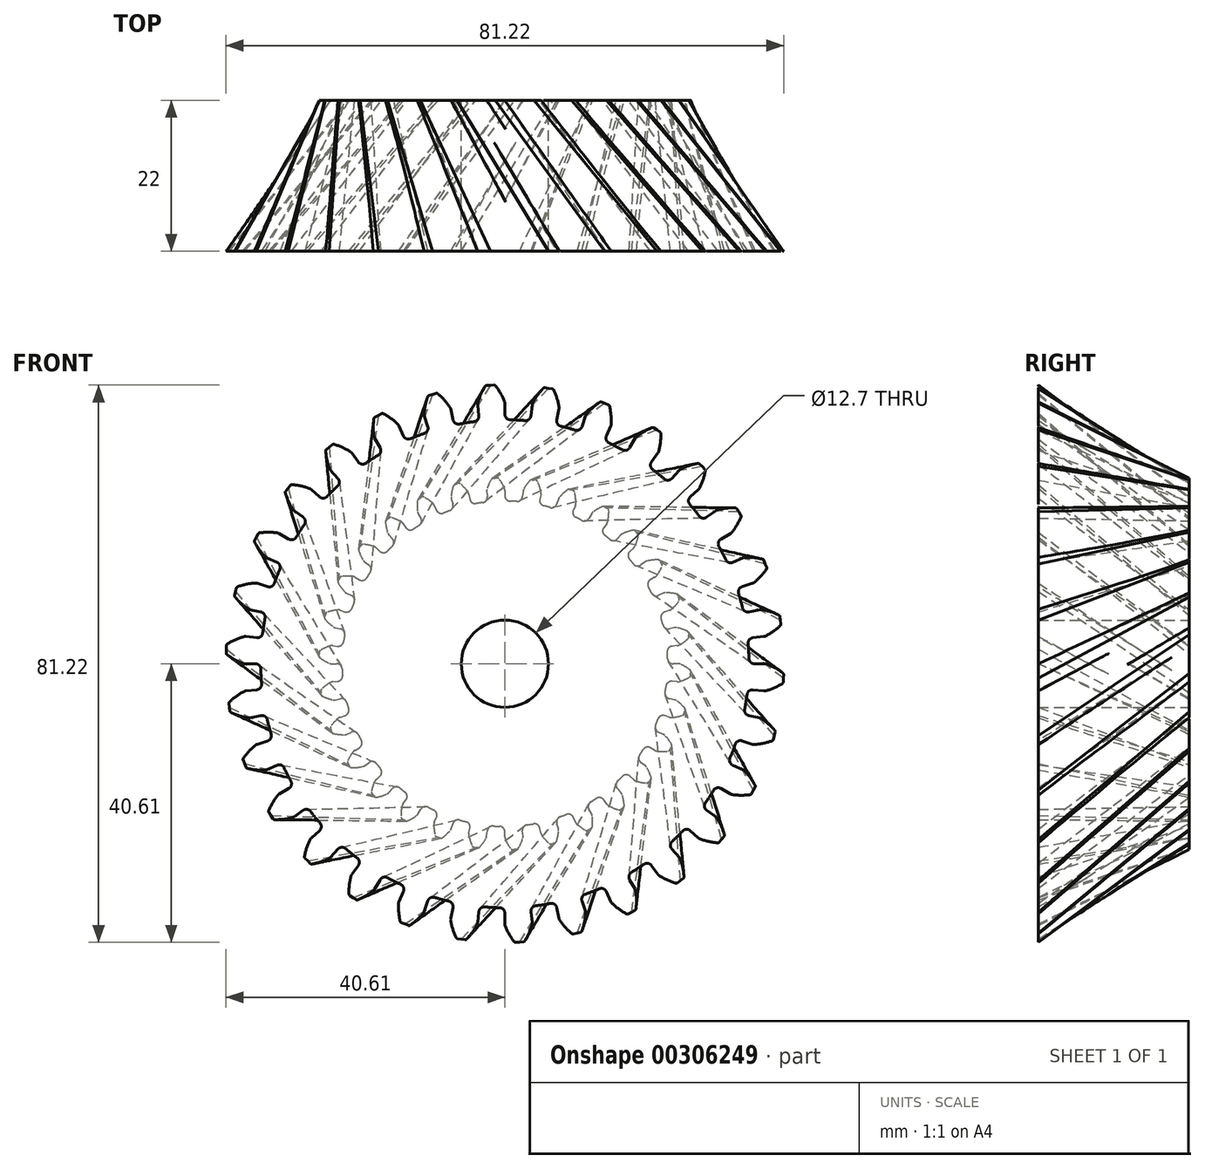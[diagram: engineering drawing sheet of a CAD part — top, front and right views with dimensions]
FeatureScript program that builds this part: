
annotation { "Feature Type Name" : "Feature", "Feature Type Description" : "" }
export const myFeature = defineFeature(function(context is Context, id is Id, definition is map)
    precondition{}
    {
        {
            var Q0;
            Q0=qCreatedBy(makeId("Front.planeOp"),FACE);
            var sketch = newSketch(context, id + "F0", { "sketchPlane" : qUnion([Q0])});
            skArc(sketch, "E0", {"start": v(-3.24, 23.49) * mm, "mid": v(-4.09, 23.36) * mm, "end": v(-4.93, 23.2) * mm});
            skArc(sketch, "E1.trimOffspring", {"start": v(-0.06, 25.55) * mm, "mid": v(-0.42, 26.29) * mm, "end": v(-0.88, 26.97) * mm});
            skLineSegment(sketch, "E2", {"start": v(-1.08, 27.07) * mm, "end": v(-1.42, 27.07) * mm});
            skLineSegment(sketch, "E3", {"start": v(0, 25.25) * mm, "end": v(0, 24.5) * mm});
            skLineSegment(sketch, "E4.MirrorCS", {"start": v(-1.76, 27.04) * mm, "end": v(-1.42, 27.07) * mm});
            skArc(sketch, "E5.MirrorCS", {"start": v(-2.61, 25.42) * mm, "mid": v(-2.33, 26.19) * mm, "end": v(-1.95, 26.92) * mm});
            skLineSegment(sketch, "E6.MirrorCS", {"start": v(-2.64, 25.1) * mm, "end": v(-2.56, 24.36) * mm});
            skArc(sketch, "E7.filletArc", {"start": v(-3.24, 23.49) * mm, "mid": v(-2.72, 23.79) * mm, "end": v(-2.56, 24.36) * mm});
            skPoint(sketch, "E8.visualSharp", {"position": v(0, 23.71) * mm});
            skPoint(sketch, "E9.visualSharp", {"position": v(-2.66, 25.26) * mm});
            skArc(sketch, "E9.filletArc", {"start": v(-2.65, 25.26) * mm, "mid": v(-2.65, 25.26) * mm, "end": v(-2.65, 25.26) * mm});
            skArc(sketch, "E10.filletArc", {"start": v(0, 24.5) * mm, "mid": v(0.22, 23.94) * mm, "end": v(0.77, 23.7) * mm});
            skArc(sketch, "E11.filletArc", {"start": v(-2.61, 25.42) * mm, "mid": v(-2.64, 25.26) * mm, "end": v(-2.64, 25.1) * mm});
            skPoint(sketch, "E12.visualSharp", {"position": v(0, 25.4) * mm});
            skArc(sketch, "E12.filletArc", {"start": v(0, 25.25) * mm, "mid": v(-0.02, 25.4) * mm, "end": v(-0.06, 25.55) * mm});
            skPoint(sketch, "E13.visualSharp", {"position": v(-1.88, 27.02) * mm});
            skArc(sketch, "E13.filletArc", {"start": v(-1.76, 27.04) * mm, "mid": v(-1.86, 27) * mm, "end": v(-1.95, 26.92) * mm});
            skPoint(sketch, "E14.visualSharp", {"position": v(-0.96, 27.07) * mm});
            skArc(sketch, "E14.filletArc", {"start": v(-0.88, 26.97) * mm, "mid": v(-0.97, 27.05) * mm, "end": v(-1.08, 27.07) * mm});
            skArc(sketch, "E15.1.0", {"start": v(-5.37, 24.98) * mm, "mid": v(-5.88, 25.63) * mm, "end": v(-6.47, 26.2) * mm});
            skPoint(sketch, "E15.1.1", {"position": v(-5.28, 24.84) * mm});
            skPoint(sketch, "E15.1.2", {"position": v(-7.85, 24.16) * mm});
            skLineSegment(sketch, "E15.1.3", {"start": v(-5.25, 24.7) * mm, "end": v(-5.1, 23.96) * mm});
            skArc(sketch, "E15.1.4", {"start": v(-7.84, 24.32) * mm, "mid": v(-7.72, 25.13) * mm, "end": v(-7.5, 25.92) * mm});
            skArc(sketch, "E15.1.5", {"start": v(-8.05, 22.3) * mm, "mid": v(-7.61, 22.7) * mm, "end": v(-7.57, 23.3) * mm});
            skPoint(sketch, "E15.1.6", {"position": v(-4.93, 23.2) * mm});
            skArc(sketch, "E15.1.7", {"start": v(-5.1, 23.96) * mm, "mid": v(-4.76, 23.46) * mm, "end": v(-4.18, 23.34) * mm});
            skPoint(sketch, "E15.1.8", {"position": v(-6.56, 26.28) * mm});
            skPoint(sketch, "E15.1.9", {"position": v(-7.46, 26.04) * mm});
            skLineSegment(sketch, "E15.1.10", {"start": v(-7.8, 24.01) * mm, "end": v(-7.57, 23.3) * mm});
            skArc(sketch, "E15.1.11", {"start": v(-5.25, 24.7) * mm, "mid": v(-5.3, 24.84) * mm, "end": v(-5.37, 24.98) * mm});
            skLineSegment(sketch, "E15.1.12", {"start": v(-7.34, 26.08) * mm, "end": v(-7.02, 26.19) * mm});
            skLineSegment(sketch, "E15.1.13", {"start": v(-6.69, 26.26) * mm, "end": v(-7.02, 26.19) * mm});
            skArc(sketch, "E15.1.14", {"start": v(-7.34, 26.08) * mm, "mid": v(-7.44, 26.02) * mm, "end": v(-7.5, 25.92) * mm});
            skArc(sketch, "E15.1.15", {"start": v(-6.47, 26.2) * mm, "mid": v(-6.57, 26.25) * mm, "end": v(-6.69, 26.26) * mm});
            skArc(sketch, "E15.1.16", {"start": v(-7.84, 24.32) * mm, "mid": v(-7.84, 24.16) * mm, "end": v(-7.8, 24.01) * mm});
            skArc(sketch, "E15.1.17", {"start": v(-7.85, 24.16) * mm, "mid": v(-7.85, 24.16) * mm, "end": v(-7.85, 24.15) * mm});
            skArc(sketch, "E15.1.18", {"start": v(-7.85, 24.16) * mm, "mid": v(-7.85, 24.16) * mm, "end": v(-7.85, 24.15) * mm});
            skArc(sketch, "E15.2.0", {"start": v(-10.45, 23.32) * mm, "mid": v(-11.08, 23.84) * mm, "end": v(-11.77, 24.28) * mm});
            skPoint(sketch, "E15.2.1", {"position": v(-10.33, 23.2) * mm});
            skPoint(sketch, "E15.2.2", {"position": v(-12.7, 22) * mm});
            skLineSegment(sketch, "E15.2.3", {"start": v(-10.27, 23.06) * mm, "end": v(-9.96, 22.37) * mm});
            skArc(sketch, "E15.2.4", {"start": v(-12.72, 22.16) * mm, "mid": v(-12.78, 22.98) * mm, "end": v(-12.73, 23.8) * mm});
            skArc(sketch, "E15.2.5", {"start": v(-12.51, 20.14) * mm, "mid": v(-12.16, 20.62) * mm, "end": v(-12.25, 21.21) * mm});
            skPoint(sketch, "E15.2.6", {"position": v(-9.64, 21.66) * mm});
            skArc(sketch, "E15.2.7", {"start": v(-9.96, 22.37) * mm, "mid": v(-9.53, 21.96) * mm, "end": v(-8.94, 21.96) * mm});
            skPoint(sketch, "E15.2.8", {"position": v(-11.88, 24.34) * mm});
            skPoint(sketch, "E15.2.9", {"position": v(-12.7, 23.92) * mm});
            skLineSegment(sketch, "E15.2.10", {"start": v(-12.62, 21.87) * mm, "end": v(-12.25, 21.21) * mm});
            skArc(sketch, "E15.2.11", {"start": v(-10.27, 23.06) * mm, "mid": v(-10.35, 23.2) * mm, "end": v(-10.45, 23.32) * mm});
            skLineSegment(sketch, "E15.2.12", {"start": v(-12.6, 23.99) * mm, "end": v(-12.3, 24.15) * mm});
            skLineSegment(sketch, "E15.2.13", {"start": v(-12, 24.3) * mm, "end": v(-12.3, 24.15) * mm});
            skArc(sketch, "E15.2.14", {"start": v(-12.6, 23.99) * mm, "mid": v(-12.68, 23.9) * mm, "end": v(-12.73, 23.8) * mm});
            skArc(sketch, "E15.2.15", {"start": v(-11.77, 24.28) * mm, "mid": v(-11.88, 24.31) * mm, "end": v(-12, 24.3) * mm});
            skArc(sketch, "E15.2.16", {"start": v(-12.72, 22.16) * mm, "mid": v(-12.69, 22) * mm, "end": v(-12.62, 21.87) * mm});
            skArc(sketch, "E15.2.17", {"start": v(-12.7, 22) * mm, "mid": v(-12.7, 22) * mm, "end": v(-12.7, 22) * mm});
            skArc(sketch, "E15.2.18", {"start": v(-12.7, 22) * mm, "mid": v(-12.7, 22) * mm, "end": v(-12.7, 22) * mm});
            skArc(sketch, "E16.1.3.0", {"start": v(-15.07, 20.64) * mm, "mid": v(-15.8, 21.02) * mm, "end": v(-16.56, 21.3) * mm});
            skPoint(sketch, "E16.4.3.0", {"position": v(-14.93, 20.55) * mm});
            skPoint(sketch, "E16.5.3.0", {"position": v(-17, 18.88) * mm});
            skLineSegment(sketch, "E16.6.3.0", {"start": v(-14.84, 20.43) * mm, "end": v(-14.4, 19.81) * mm});
            skArc(sketch, "E16.9.3.0", {"start": v(-17.05, 19.03) * mm, "mid": v(-17.28, 19.82) * mm, "end": v(-17.4, 20.63) * mm});
            skArc(sketch, "E16.13.3.0", {"start": v(-16.43, 17.1) * mm, "mid": v(-16.18, 17.64) * mm, "end": v(-16.39, 18.2) * mm});
            skPoint(sketch, "E16.17.3.0", {"position": v(-13.94, 19.18) * mm});
            skArc(sketch, "E16.18.3.0", {"start": v(-14.4, 19.81) * mm, "mid": v(-13.9, 19.5) * mm, "end": v(-13.3, 19.62) * mm});
            skPoint(sketch, "E16.22.3.0", {"position": v(-16.69, 21.34) * mm});
            skPoint(sketch, "E16.23.3.0", {"position": v(-17.4, 20.76) * mm});
            skLineSegment(sketch, "E16.24.3.0", {"start": v(-16.9, 18.76) * mm, "end": v(-16.39, 18.2) * mm});
            skArc(sketch, "E16.27.3.0", {"start": v(-14.84, 20.43) * mm, "mid": v(-14.94, 20.54) * mm, "end": v(-15.07, 20.64) * mm});
            skLineSegment(sketch, "E16.31.3.0", {"start": v(-17.31, 20.84) * mm, "end": v(-17.06, 21.07) * mm});
            skLineSegment(sketch, "E16.34.3.0", {"start": v(-16.79, 21.27) * mm, "end": v(-17.06, 21.07) * mm});
            skArc(sketch, "E16.37.3.0", {"start": v(-17.31, 20.84) * mm, "mid": v(-17.38, 20.75) * mm, "end": v(-17.4, 20.63) * mm});
            skArc(sketch, "E16.41.3.0", {"start": v(-16.56, 21.3) * mm, "mid": v(-16.68, 21.31) * mm, "end": v(-16.79, 21.27) * mm});
            skArc(sketch, "E16.45.3.0", {"start": v(-17.05, 19.03) * mm, "mid": v(-16.99, 18.89) * mm, "end": v(-16.9, 18.76) * mm});
            skArc(sketch, "E16.49.3.0", {"start": v(-17, 18.88) * mm, "mid": v(-17, 18.88) * mm, "end": v(-17, 18.87) * mm});
            skArc(sketch, "E16.53.3.0", {"start": v(-17, 18.88) * mm, "mid": v(-17, 18.88) * mm, "end": v(-17, 18.87) * mm});
            skArc(sketch, "E16.1.4.0", {"start": v(-19.03, 17.05) * mm, "mid": v(-19.82, 17.28) * mm, "end": v(-20.63, 17.4) * mm});
            skPoint(sketch, "E16.4.4.0", {"position": v(-18.88, 17) * mm});
            skPoint(sketch, "E16.5.4.0", {"position": v(-20.55, 14.93) * mm});
            skLineSegment(sketch, "E16.6.4.0", {"start": v(-18.76, 16.9) * mm, "end": v(-18.2, 16.39) * mm});
            skArc(sketch, "E16.9.4.0", {"start": v(-20.64, 15.07) * mm, "mid": v(-21.02, 15.8) * mm, "end": v(-21.3, 16.56) * mm});
            skArc(sketch, "E16.13.4.0", {"start": v(-19.62, 13.3) * mm, "mid": v(-19.5, 13.9) * mm, "end": v(-19.81, 14.4) * mm});
            skPoint(sketch, "E16.17.4.0", {"position": v(-17.62, 15.87) * mm});
            skArc(sketch, "E16.18.4.0", {"start": v(-18.2, 16.39) * mm, "mid": v(-17.64, 16.18) * mm, "end": v(-17.1, 16.43) * mm});
            skPoint(sketch, "E16.22.4.0", {"position": v(-20.76, 17.4) * mm});
            skPoint(sketch, "E16.23.4.0", {"position": v(-21.34, 16.69) * mm});
            skLineSegment(sketch, "E16.24.4.0", {"start": v(-20.43, 14.84) * mm, "end": v(-19.81, 14.4) * mm});
            skArc(sketch, "E16.27.4.0", {"start": v(-18.76, 16.9) * mm, "mid": v(-18.89, 16.99) * mm, "end": v(-19.03, 17.05) * mm});
            skLineSegment(sketch, "E16.31.4.0", {"start": v(-21.27, 16.79) * mm, "end": v(-21.07, 17.06) * mm});
            skLineSegment(sketch, "E16.34.4.0", {"start": v(-20.84, 17.31) * mm, "end": v(-21.07, 17.06) * mm});
            skArc(sketch, "E16.37.4.0", {"start": v(-21.27, 16.79) * mm, "mid": v(-21.31, 16.68) * mm, "end": v(-21.3, 16.56) * mm});
            skArc(sketch, "E16.41.4.0", {"start": v(-20.63, 17.4) * mm, "mid": v(-20.75, 17.38) * mm, "end": v(-20.84, 17.31) * mm});
            skArc(sketch, "E16.45.4.0", {"start": v(-20.64, 15.07) * mm, "mid": v(-20.54, 14.94) * mm, "end": v(-20.43, 14.84) * mm});
            skArc(sketch, "E16.49.4.0", {"start": v(-20.55, 14.93) * mm, "mid": v(-20.55, 14.93) * mm, "end": v(-20.55, 14.93) * mm});
            skArc(sketch, "E16.53.4.0", {"start": v(-20.55, 14.93) * mm, "mid": v(-20.55, 14.93) * mm, "end": v(-20.55, 14.93) * mm});
            skArc(sketch, "E16.1.5.0", {"start": v(-22.16, 12.72) * mm, "mid": v(-22.98, 12.78) * mm, "end": v(-23.8, 12.73) * mm});
            skPoint(sketch, "E16.4.5.0", {"position": v(-22, 12.7) * mm});
            skPoint(sketch, "E16.5.5.0", {"position": v(-23.2, 10.33) * mm});
            skLineSegment(sketch, "E16.6.5.0", {"start": v(-21.87, 12.62) * mm, "end": v(-21.21, 12.25) * mm});
            skArc(sketch, "E16.9.5.0", {"start": v(-23.32, 10.45) * mm, "mid": v(-23.84, 11.08) * mm, "end": v(-24.28, 11.77) * mm});
            skArc(sketch, "E16.13.5.0", {"start": v(-21.96, 8.94) * mm, "mid": v(-21.96, 9.53) * mm, "end": v(-22.37, 9.96) * mm});
            skPoint(sketch, "E16.17.5.0", {"position": v(-20.53, 11.86) * mm});
            skArc(sketch, "E16.18.5.0", {"start": v(-21.21, 12.25) * mm, "mid": v(-20.62, 12.16) * mm, "end": v(-20.14, 12.51) * mm});
            skPoint(sketch, "E16.22.5.0", {"position": v(-23.92, 12.7) * mm});
            skPoint(sketch, "E16.23.5.0", {"position": v(-24.34, 11.88) * mm});
            skLineSegment(sketch, "E16.24.5.0", {"start": v(-23.06, 10.27) * mm, "end": v(-22.37, 9.96) * mm});
            skArc(sketch, "E16.27.5.0", {"start": v(-21.87, 12.62) * mm, "mid": v(-22, 12.69) * mm, "end": v(-22.16, 12.72) * mm});
            skLineSegment(sketch, "E16.31.5.0", {"start": v(-24.3, 12) * mm, "end": v(-24.15, 12.3) * mm});
            skLineSegment(sketch, "E16.34.5.0", {"start": v(-23.99, 12.6) * mm, "end": v(-24.15, 12.3) * mm});
            skArc(sketch, "E16.37.5.0", {"start": v(-24.3, 12) * mm, "mid": v(-24.31, 11.88) * mm, "end": v(-24.28, 11.77) * mm});
            skArc(sketch, "E16.41.5.0", {"start": v(-23.8, 12.73) * mm, "mid": v(-23.9, 12.68) * mm, "end": v(-23.99, 12.6) * mm});
            skArc(sketch, "E16.45.5.0", {"start": v(-23.32, 10.45) * mm, "mid": v(-23.2, 10.35) * mm, "end": v(-23.06, 10.27) * mm});
            skArc(sketch, "E16.49.5.0", {"start": v(-23.2, 10.33) * mm, "mid": v(-23.2, 10.33) * mm, "end": v(-23.2, 10.33) * mm});
            skArc(sketch, "E16.53.5.0", {"start": v(-23.2, 10.33) * mm, "mid": v(-23.2, 10.33) * mm, "end": v(-23.2, 10.33) * mm});
            skArc(sketch, "E16.1.6.0", {"start": v(-24.32, 7.84) * mm, "mid": v(-25.13, 7.72) * mm, "end": v(-25.92, 7.5) * mm});
            skPoint(sketch, "E16.4.6.0", {"position": v(-24.16, 7.85) * mm});
            skPoint(sketch, "E16.5.6.0", {"position": v(-24.84, 5.28) * mm});
            skLineSegment(sketch, "E16.6.6.0", {"start": v(-24.01, 7.8) * mm, "end": v(-23.3, 7.57) * mm});
            skArc(sketch, "E16.9.6.0", {"start": v(-24.98, 5.37) * mm, "mid": v(-25.63, 5.88) * mm, "end": v(-26.2, 6.47) * mm});
            skArc(sketch, "E16.13.6.0", {"start": v(-23.34, 4.18) * mm, "mid": v(-23.46, 4.76) * mm, "end": v(-23.96, 5.1) * mm});
            skPoint(sketch, "E16.17.6.0", {"position": v(-22.55, 7.33) * mm});
            skArc(sketch, "E16.18.6.0", {"start": v(-23.3, 7.57) * mm, "mid": v(-22.7, 7.61) * mm, "end": v(-22.3, 8.05) * mm});
            skPoint(sketch, "E16.22.6.0", {"position": v(-26.04, 7.46) * mm});
            skPoint(sketch, "E16.23.6.0", {"position": v(-26.28, 6.56) * mm});
            skLineSegment(sketch, "E16.24.6.0", {"start": v(-24.7, 5.25) * mm, "end": v(-23.96, 5.1) * mm});
            skArc(sketch, "E16.27.6.0", {"start": v(-24.01, 7.8) * mm, "mid": v(-24.16, 7.84) * mm, "end": v(-24.32, 7.84) * mm});
            skLineSegment(sketch, "E16.31.6.0", {"start": v(-26.26, 6.69) * mm, "end": v(-26.19, 7.02) * mm});
            skLineSegment(sketch, "E16.34.6.0", {"start": v(-26.08, 7.34) * mm, "end": v(-26.19, 7.02) * mm});
            skArc(sketch, "E16.37.6.0", {"start": v(-26.26, 6.69) * mm, "mid": v(-26.25, 6.57) * mm, "end": v(-26.2, 6.47) * mm});
            skArc(sketch, "E16.41.6.0", {"start": v(-25.92, 7.5) * mm, "mid": v(-26.02, 7.44) * mm, "end": v(-26.08, 7.34) * mm});
            skArc(sketch, "E16.45.6.0", {"start": v(-24.98, 5.37) * mm, "mid": v(-24.84, 5.3) * mm, "end": v(-24.7, 5.25) * mm});
            skArc(sketch, "E16.49.6.0", {"start": v(-24.85, 5.28) * mm, "mid": v(-24.84, 5.28) * mm, "end": v(-24.84, 5.28) * mm});
            skArc(sketch, "E16.53.6.0", {"start": v(-24.85, 5.28) * mm, "mid": v(-24.84, 5.28) * mm, "end": v(-24.84, 5.28) * mm});
            skArc(sketch, "E16.1.7.0", {"start": v(-25.42, 2.61) * mm, "mid": v(-26.19, 2.33) * mm, "end": v(-26.92, 1.95) * mm});
            skPoint(sketch, "E16.4.7.0", {"position": v(-25.26, 2.66) * mm});
            skPoint(sketch, "E16.5.7.0", {"position": v(-25.4, 0) * mm});
            skLineSegment(sketch, "E16.6.7.0", {"start": v(-25.1, 2.64) * mm, "end": v(-24.36, 2.56) * mm});
            skArc(sketch, "E16.9.7.0", {"start": v(-25.55, 0.06) * mm, "mid": v(-26.29, 0.42) * mm, "end": v(-26.97, 0.88) * mm});
            skArc(sketch, "E16.13.7.0", {"start": v(-23.7, -0.77) * mm, "mid": v(-23.94, -0.22) * mm, "end": v(-24.5, 0) * mm});
            skPoint(sketch, "E16.17.7.0", {"position": v(-23.58, 2.48) * mm});
            skArc(sketch, "E16.18.7.0", {"start": v(-24.36, 2.56) * mm, "mid": v(-23.79, 2.72) * mm, "end": v(-23.49, 3.24) * mm});
            skPoint(sketch, "E16.22.7.0", {"position": v(-27.02, 1.88) * mm});
            skPoint(sketch, "E16.23.7.0", {"position": v(-27.07, 0.96) * mm});
            skLineSegment(sketch, "E16.24.7.0", {"start": v(-25.25, 0) * mm, "end": v(-24.5, 0) * mm});
            skArc(sketch, "E16.27.7.0", {"start": v(-25.1, 2.64) * mm, "mid": v(-25.26, 2.64) * mm, "end": v(-25.42, 2.61) * mm});
            skLineSegment(sketch, "E16.31.7.0", {"start": v(-27.07, 1.08) * mm, "end": v(-27.07, 1.42) * mm});
            skLineSegment(sketch, "E16.34.7.0", {"start": v(-27.04, 1.76) * mm, "end": v(-27.07, 1.42) * mm});
            skArc(sketch, "E16.37.7.0", {"start": v(-27.07, 1.08) * mm, "mid": v(-27.05, 0.97) * mm, "end": v(-26.97, 0.88) * mm});
            skArc(sketch, "E16.41.7.0", {"start": v(-26.92, 1.95) * mm, "mid": v(-27, 1.86) * mm, "end": v(-27.04, 1.76) * mm});
            skArc(sketch, "E16.45.7.0", {"start": v(-25.55, 0.06) * mm, "mid": v(-25.4, 0.02) * mm, "end": v(-25.25, 0) * mm});
            skArc(sketch, "E16.49.7.0", {"start": v(-25.4, 0) * mm, "mid": v(-25.4, 0) * mm, "end": v(-25.4, 0) * mm});
            skArc(sketch, "E16.53.7.0", {"start": v(-25.4, 0) * mm, "mid": v(-25.4, 0) * mm, "end": v(-25.4, 0) * mm});
            skArc(sketch, "E16.1.8.0", {"start": v(-25.4, -2.73) * mm, "mid": v(-26.1, -3.17) * mm, "end": v(-26.73, -3.7) * mm});
            skPoint(sketch, "E16.4.8.0", {"position": v(-25.26, -2.66) * mm});
            skPoint(sketch, "E16.5.8.0", {"position": v(-24.84, -5.28) * mm});
            skLineSegment(sketch, "E16.6.8.0", {"start": v(-25.1, -2.64) * mm, "end": v(-24.36, -2.56) * mm});
            skArc(sketch, "E16.9.8.0", {"start": v(-25, -5.25) * mm, "mid": v(-25.8, -5.05) * mm, "end": v(-26.57, -4.75) * mm});
            skArc(sketch, "E16.13.8.0", {"start": v(-23.02, -5.68) * mm, "mid": v(-23.37, -5.2) * mm, "end": v(-23.96, -5.1) * mm});
            skPoint(sketch, "E16.17.8.0", {"position": v(-23.58, -2.48) * mm});
            skArc(sketch, "E16.18.8.0", {"start": v(-24.36, -2.56) * mm, "mid": v(-23.83, -2.28) * mm, "end": v(-23.65, -1.71) * mm});
            skPoint(sketch, "E16.22.8.0", {"position": v(-26.82, -3.78) * mm});
            skPoint(sketch, "E16.23.8.0", {"position": v(-26.68, -4.7) * mm});
            skLineSegment(sketch, "E16.24.8.0", {"start": v(-24.7, -5.25) * mm, "end": v(-23.96, -5.1) * mm});
            skArc(sketch, "E16.27.8.0", {"start": v(-25.1, -2.64) * mm, "mid": v(-25.26, -2.67) * mm, "end": v(-25.4, -2.73) * mm});
            skLineSegment(sketch, "E16.31.8.0", {"start": v(-26.7, -4.57) * mm, "end": v(-26.78, -4.24) * mm});
            skLineSegment(sketch, "E16.34.8.0", {"start": v(-26.81, -3.9) * mm, "end": v(-26.78, -4.24) * mm});
            skArc(sketch, "E16.37.8.0", {"start": v(-26.7, -4.57) * mm, "mid": v(-26.66, -4.68) * mm, "end": v(-26.57, -4.75) * mm});
            skArc(sketch, "E16.41.8.0", {"start": v(-26.73, -3.7) * mm, "mid": v(-26.8, -3.79) * mm, "end": v(-26.81, -3.9) * mm});
            skArc(sketch, "E16.45.8.0", {"start": v(-25, -5.25) * mm, "mid": v(-24.85, -5.27) * mm, "end": v(-24.7, -5.25) * mm});
            skArc(sketch, "E16.49.8.0", {"start": v(-24.85, -5.28) * mm, "mid": v(-24.84, -5.28) * mm, "end": v(-24.84, -5.28) * mm});
            skArc(sketch, "E16.53.8.0", {"start": v(-24.85, -5.28) * mm, "mid": v(-24.84, -5.28) * mm, "end": v(-24.84, -5.28) * mm});
            skArc(sketch, "E16.1.9.0", {"start": v(-24.28, -7.95) * mm, "mid": v(-24.87, -8.53) * mm, "end": v(-25.38, -9.17) * mm});
            skPoint(sketch, "E16.4.9.0", {"position": v(-24.16, -7.85) * mm});
            skPoint(sketch, "E16.5.9.0", {"position": v(-23.2, -10.33) * mm});
            skLineSegment(sketch, "E16.6.9.0", {"start": v(-24.01, -7.8) * mm, "end": v(-23.3, -7.57) * mm});
            skArc(sketch, "E16.9.9.0", {"start": v(-23.37, -10.34) * mm, "mid": v(-24.19, -10.3) * mm, "end": v(-25, -10.17) * mm});
            skArc(sketch, "E16.13.9.0", {"start": v(-21.34, -10.34) * mm, "mid": v(-21.78, -9.94) * mm, "end": v(-22.37, -9.96) * mm});
            skPoint(sketch, "E16.17.9.0", {"position": v(-22.55, -7.33) * mm});
            skArc(sketch, "E16.18.9.0", {"start": v(-23.3, -7.57) * mm, "mid": v(-22.84, -7.19) * mm, "end": v(-22.78, -6.6) * mm});
            skPoint(sketch, "E16.22.9.0", {"position": v(-25.45, -9.28) * mm});
            skPoint(sketch, "E16.23.9.0", {"position": v(-25.12, -10.14) * mm});
            skLineSegment(sketch, "E16.24.9.0", {"start": v(-23.06, -10.27) * mm, "end": v(-22.37, -9.96) * mm});
            skArc(sketch, "E16.27.9.0", {"start": v(-24.01, -7.8) * mm, "mid": v(-24.15, -7.86) * mm, "end": v(-24.28, -7.95) * mm});
            skLineSegment(sketch, "E16.31.9.0", {"start": v(-25.17, -10.02) * mm, "end": v(-25.3, -9.72) * mm});
            skLineSegment(sketch, "E16.34.9.0", {"start": v(-25.41, -9.4) * mm, "end": v(-25.3, -9.72) * mm});
            skArc(sketch, "E16.37.9.0", {"start": v(-25.17, -10.02) * mm, "mid": v(-25.1, -10.12) * mm, "end": v(-25, -10.17) * mm});
            skArc(sketch, "E16.41.9.0", {"start": v(-25.38, -9.17) * mm, "mid": v(-25.42, -9.28) * mm, "end": v(-25.41, -9.4) * mm});
            skArc(sketch, "E16.45.9.0", {"start": v(-23.37, -10.34) * mm, "mid": v(-23.21, -10.32) * mm, "end": v(-23.06, -10.27) * mm});
            skArc(sketch, "E16.49.9.0", {"start": v(-23.2, -10.33) * mm, "mid": v(-23.2, -10.33) * mm, "end": v(-23.2, -10.33) * mm});
            skArc(sketch, "E16.53.9.0", {"start": v(-23.2, -10.33) * mm, "mid": v(-23.2, -10.33) * mm, "end": v(-23.2, -10.33) * mm});
            skArc(sketch, "E16.1.10.0", {"start": v(-22.1, -12.83) * mm, "mid": v(-22.55, -13.51) * mm, "end": v(-22.92, -14.25) * mm});
            skPoint(sketch, "E16.4.10.0", {"position": v(-22, -12.7) * mm});
            skPoint(sketch, "E16.5.10.0", {"position": v(-20.55, -14.93) * mm});
            skLineSegment(sketch, "E16.6.10.0", {"start": v(-21.87, -12.62) * mm, "end": v(-21.21, -12.25) * mm});
            skArc(sketch, "E16.9.10.0", {"start": v(-20.7, -14.97) * mm, "mid": v(-21.52, -15.1) * mm, "end": v(-22.34, -15.14) * mm});
            skArc(sketch, "E16.13.10.0", {"start": v(-18.72, -14.55) * mm, "mid": v(-19.24, -14.25) * mm, "end": v(-19.81, -14.4) * mm});
            skPoint(sketch, "E16.17.10.0", {"position": v(-20.53, -11.86) * mm});
            skArc(sketch, "E16.18.10.0", {"start": v(-21.21, -12.25) * mm, "mid": v(-20.84, -11.78) * mm, "end": v(-20.9, -11.18) * mm});
            skPoint(sketch, "E16.22.10.0", {"position": v(-22.97, -14.36) * mm});
            skPoint(sketch, "E16.23.10.0", {"position": v(-22.46, -15.14) * mm});
            skLineSegment(sketch, "E16.24.10.0", {"start": v(-20.43, -14.84) * mm, "end": v(-19.81, -14.4) * mm});
            skArc(sketch, "E16.27.10.0", {"start": v(-21.87, -12.62) * mm, "mid": v(-22, -12.71) * mm, "end": v(-22.1, -12.83) * mm});
            skLineSegment(sketch, "E16.31.10.0", {"start": v(-22.54, -15.04) * mm, "end": v(-22.74, -14.76) * mm});
            skLineSegment(sketch, "E16.34.10.0", {"start": v(-22.9, -14.47) * mm, "end": v(-22.74, -14.76) * mm});
            skArc(sketch, "E16.37.10.0", {"start": v(-22.54, -15.04) * mm, "mid": v(-22.45, -15.11) * mm, "end": v(-22.34, -15.14) * mm});
            skArc(sketch, "E16.41.10.0", {"start": v(-22.92, -14.25) * mm, "mid": v(-22.94, -14.36) * mm, "end": v(-22.9, -14.47) * mm});
            skArc(sketch, "E16.45.10.0", {"start": v(-20.7, -14.97) * mm, "mid": v(-20.56, -14.92) * mm, "end": v(-20.43, -14.84) * mm});
            skArc(sketch, "E16.49.10.0", {"start": v(-20.55, -14.93) * mm, "mid": v(-20.55, -14.93) * mm, "end": v(-20.55, -14.93) * mm});
            skArc(sketch, "E16.53.10.0", {"start": v(-20.55, -14.93) * mm, "mid": v(-20.55, -14.93) * mm, "end": v(-20.55, -14.93) * mm});
            skArc(sketch, "E16.1.11.0", {"start": v(-18.95, -17.14) * mm, "mid": v(-19.25, -17.9) * mm, "end": v(-19.46, -18.7) * mm});
            skPoint(sketch, "E16.4.11.0", {"position": v(-18.88, -17) * mm});
            skPoint(sketch, "E16.5.11.0", {"position": v(-17, -18.88) * mm});
            skLineSegment(sketch, "E16.6.11.0", {"start": v(-18.76, -16.9) * mm, "end": v(-18.2, -16.39) * mm});
            skArc(sketch, "E16.9.11.0", {"start": v(-17.14, -18.95) * mm, "mid": v(-17.9, -19.25) * mm, "end": v(-18.7, -19.46) * mm});
            skArc(sketch, "E16.13.11.0", {"start": v(-15.29, -18.13) * mm, "mid": v(-15.85, -17.94) * mm, "end": v(-16.39, -18.2) * mm});
            skPoint(sketch, "E16.17.11.0", {"position": v(-17.62, -15.87) * mm});
            skArc(sketch, "E16.18.11.0", {"start": v(-18.2, -16.39) * mm, "mid": v(-17.94, -15.85) * mm, "end": v(-18.13, -15.29) * mm});
            skPoint(sketch, "E16.22.11.0", {"position": v(-19.48, -18.83) * mm});
            skPoint(sketch, "E16.23.11.0", {"position": v(-18.83, -19.48) * mm});
            skLineSegment(sketch, "E16.24.11.0", {"start": v(-16.9, -18.76) * mm, "end": v(-16.39, -18.2) * mm});
            skArc(sketch, "E16.27.11.0", {"start": v(-18.76, -16.9) * mm, "mid": v(-18.87, -17) * mm, "end": v(-18.95, -17.14) * mm});
            skLineSegment(sketch, "E16.31.11.0", {"start": v(-18.92, -19.4) * mm, "end": v(-19.17, -19.17) * mm});
            skLineSegment(sketch, "E16.34.11.0", {"start": v(-19.4, -18.92) * mm, "end": v(-19.17, -19.17) * mm});
            skArc(sketch, "E16.37.11.0", {"start": v(-18.92, -19.4) * mm, "mid": v(-18.82, -19.45) * mm, "end": v(-18.7, -19.46) * mm});
            skArc(sketch, "E16.41.11.0", {"start": v(-19.46, -18.7) * mm, "mid": v(-19.45, -18.82) * mm, "end": v(-19.4, -18.92) * mm});
            skArc(sketch, "E16.45.11.0", {"start": v(-17.14, -18.95) * mm, "mid": v(-17, -18.87) * mm, "end": v(-16.9, -18.76) * mm});
            skArc(sketch, "E16.49.11.0", {"start": v(-17, -18.88) * mm, "mid": v(-17, -18.88) * mm, "end": v(-17, -18.87) * mm});
            skArc(sketch, "E16.53.11.0", {"start": v(-17, -18.88) * mm, "mid": v(-17, -18.88) * mm, "end": v(-17, -18.87) * mm});
            skArc(sketch, "E16.1.12.0", {"start": v(-14.97, -20.7) * mm, "mid": v(-15.1, -21.52) * mm, "end": v(-15.14, -22.34) * mm});
            skPoint(sketch, "E16.4.12.0", {"position": v(-14.93, -20.55) * mm});
            skPoint(sketch, "E16.5.12.0", {"position": v(-12.7, -22) * mm});
            skLineSegment(sketch, "E16.6.12.0", {"start": v(-14.84, -20.43) * mm, "end": v(-14.4, -19.81) * mm});
            skArc(sketch, "E16.9.12.0", {"start": v(-12.83, -22.1) * mm, "mid": v(-13.51, -22.55) * mm, "end": v(-14.25, -22.92) * mm});
            skArc(sketch, "E16.13.12.0", {"start": v(-11.18, -20.9) * mm, "mid": v(-11.78, -20.84) * mm, "end": v(-12.25, -21.21) * mm});
            skPoint(sketch, "E16.17.12.0", {"position": v(-13.94, -19.18) * mm});
            skArc(sketch, "E16.18.12.0", {"start": v(-14.4, -19.81) * mm, "mid": v(-14.25, -19.24) * mm, "end": v(-14.55, -18.72) * mm});
            skPoint(sketch, "E16.22.12.0", {"position": v(-15.14, -22.46) * mm});
            skPoint(sketch, "E16.23.12.0", {"position": v(-14.36, -22.97) * mm});
            skLineSegment(sketch, "E16.24.12.0", {"start": v(-12.62, -21.87) * mm, "end": v(-12.25, -21.21) * mm});
            skArc(sketch, "E16.27.12.0", {"start": v(-14.84, -20.43) * mm, "mid": v(-14.92, -20.56) * mm, "end": v(-14.97, -20.7) * mm});
            skLineSegment(sketch, "E16.31.12.0", {"start": v(-14.47, -22.9) * mm, "end": v(-14.76, -22.74) * mm});
            skLineSegment(sketch, "E16.34.12.0", {"start": v(-15.04, -22.54) * mm, "end": v(-14.76, -22.74) * mm});
            skArc(sketch, "E16.37.12.0", {"start": v(-14.47, -22.9) * mm, "mid": v(-14.36, -22.94) * mm, "end": v(-14.25, -22.92) * mm});
            skArc(sketch, "E16.41.12.0", {"start": v(-15.14, -22.34) * mm, "mid": v(-15.11, -22.45) * mm, "end": v(-15.04, -22.54) * mm});
            skArc(sketch, "E16.45.12.0", {"start": v(-12.83, -22.1) * mm, "mid": v(-12.71, -22) * mm, "end": v(-12.62, -21.87) * mm});
            skArc(sketch, "E16.49.12.0", {"start": v(-12.7, -22) * mm, "mid": v(-12.7, -22) * mm, "end": v(-12.7, -22) * mm});
            skArc(sketch, "E16.53.12.0", {"start": v(-12.7, -22) * mm, "mid": v(-12.7, -22) * mm, "end": v(-12.7, -22) * mm});
            skArc(sketch, "E16.1.13.0", {"start": v(-10.34, -23.37) * mm, "mid": v(-10.3, -24.19) * mm, "end": v(-10.17, -25) * mm});
            skPoint(sketch, "E16.4.13.0", {"position": v(-10.33, -23.2) * mm});
            skPoint(sketch, "E16.5.13.0", {"position": v(-7.85, -24.16) * mm});
            skLineSegment(sketch, "E16.6.13.0", {"start": v(-10.27, -23.06) * mm, "end": v(-9.96, -22.37) * mm});
            skArc(sketch, "E16.9.13.0", {"start": v(-7.95, -24.28) * mm, "mid": v(-8.53, -24.87) * mm, "end": v(-9.17, -25.38) * mm});
            skArc(sketch, "E16.13.13.0", {"start": v(-6.6, -22.78) * mm, "mid": v(-7.19, -22.84) * mm, "end": v(-7.57, -23.3) * mm});
            skPoint(sketch, "E16.17.13.0", {"position": v(-9.64, -21.66) * mm});
            skArc(sketch, "E16.18.13.0", {"start": v(-9.96, -22.37) * mm, "mid": v(-9.94, -21.78) * mm, "end": v(-10.34, -21.34) * mm});
            skPoint(sketch, "E16.22.13.0", {"position": v(-10.14, -25.12) * mm});
            skPoint(sketch, "E16.23.13.0", {"position": v(-9.28, -25.45) * mm});
            skLineSegment(sketch, "E16.24.13.0", {"start": v(-7.8, -24.01) * mm, "end": v(-7.57, -23.3) * mm});
            skArc(sketch, "E16.27.13.0", {"start": v(-10.27, -23.06) * mm, "mid": v(-10.32, -23.21) * mm, "end": v(-10.34, -23.37) * mm});
            skLineSegment(sketch, "E16.31.13.0", {"start": v(-9.4, -25.41) * mm, "end": v(-9.72, -25.3) * mm});
            skLineSegment(sketch, "E16.34.13.0", {"start": v(-10.02, -25.17) * mm, "end": v(-9.72, -25.3) * mm});
            skArc(sketch, "E16.37.13.0", {"start": v(-9.4, -25.41) * mm, "mid": v(-9.28, -25.42) * mm, "end": v(-9.17, -25.38) * mm});
            skArc(sketch, "E16.41.13.0", {"start": v(-10.17, -25) * mm, "mid": v(-10.12, -25.1) * mm, "end": v(-10.02, -25.17) * mm});
            skArc(sketch, "E16.45.13.0", {"start": v(-7.95, -24.28) * mm, "mid": v(-7.86, -24.15) * mm, "end": v(-7.8, -24.01) * mm});
            skArc(sketch, "E16.49.13.0", {"start": v(-7.85, -24.16) * mm, "mid": v(-7.85, -24.16) * mm, "end": v(-7.85, -24.15) * mm});
            skArc(sketch, "E16.53.13.0", {"start": v(-7.85, -24.16) * mm, "mid": v(-7.85, -24.16) * mm, "end": v(-7.85, -24.15) * mm});
            skArc(sketch, "E16.1.14.0", {"start": v(-5.25, -25) * mm, "mid": v(-5.05, -25.8) * mm, "end": v(-4.75, -26.57) * mm});
            skPoint(sketch, "E16.4.14.0", {"position": v(-5.28, -24.84) * mm});
            skPoint(sketch, "E16.5.14.0", {"position": v(-2.66, -25.26) * mm});
            skLineSegment(sketch, "E16.6.14.0", {"start": v(-5.25, -24.7) * mm, "end": v(-5.1, -23.96) * mm});
            skArc(sketch, "E16.9.14.0", {"start": v(-2.73, -25.4) * mm, "mid": v(-3.17, -26.1) * mm, "end": v(-3.7, -26.73) * mm});
            skArc(sketch, "E16.13.14.0", {"start": v(-1.71, -23.65) * mm, "mid": v(-2.28, -23.83) * mm, "end": v(-2.56, -24.36) * mm});
            skPoint(sketch, "E16.17.14.0", {"position": v(-4.93, -23.2) * mm});
            skArc(sketch, "E16.18.14.0", {"start": v(-5.1, -23.96) * mm, "mid": v(-5.2, -23.37) * mm, "end": v(-5.68, -23.02) * mm});
            skPoint(sketch, "E16.22.14.0", {"position": v(-4.7, -26.68) * mm});
            skPoint(sketch, "E16.23.14.0", {"position": v(-3.78, -26.82) * mm});
            skLineSegment(sketch, "E16.24.14.0", {"start": v(-2.64, -25.1) * mm, "end": v(-2.56, -24.36) * mm});
            skArc(sketch, "E16.27.14.0", {"start": v(-5.25, -24.7) * mm, "mid": v(-5.27, -24.85) * mm, "end": v(-5.25, -25) * mm});
            skLineSegment(sketch, "E16.31.14.0", {"start": v(-3.9, -26.81) * mm, "end": v(-4.24, -26.78) * mm});
            skLineSegment(sketch, "E16.34.14.0", {"start": v(-4.57, -26.7) * mm, "end": v(-4.24, -26.78) * mm});
            skArc(sketch, "E16.37.14.0", {"start": v(-3.9, -26.81) * mm, "mid": v(-3.79, -26.8) * mm, "end": v(-3.7, -26.73) * mm});
            skArc(sketch, "E16.41.14.0", {"start": v(-4.75, -26.57) * mm, "mid": v(-4.68, -26.66) * mm, "end": v(-4.57, -26.7) * mm});
            skArc(sketch, "E16.45.14.0", {"start": v(-2.73, -25.4) * mm, "mid": v(-2.67, -25.26) * mm, "end": v(-2.64, -25.1) * mm});
            skArc(sketch, "E16.49.14.0", {"start": v(-2.66, -25.26) * mm, "mid": v(-2.66, -25.26) * mm, "end": v(-2.65, -25.26) * mm});
            skArc(sketch, "E16.53.14.0", {"start": v(-2.66, -25.26) * mm, "mid": v(-2.66, -25.26) * mm, "end": v(-2.65, -25.26) * mm});
            skArc(sketch, "E16.1.15.0", {"start": v(0.06, -25.55) * mm, "mid": v(0.42, -26.29) * mm, "end": v(0.88, -26.97) * mm});
            skPoint(sketch, "E16.4.15.0", {"position": v(0, -25.4) * mm});
            skPoint(sketch, "E16.5.15.0", {"position": v(2.66, -25.26) * mm});
            skLineSegment(sketch, "E16.6.15.0", {"start": v(0, -25.25) * mm, "end": v(0, -24.5) * mm});
            skArc(sketch, "E16.9.15.0", {"start": v(2.61, -25.42) * mm, "mid": v(2.33, -26.19) * mm, "end": v(1.95, -26.92) * mm});
            skArc(sketch, "E16.13.15.0", {"start": v(3.24, -23.49) * mm, "mid": v(2.72, -23.79) * mm, "end": v(2.56, -24.36) * mm});
            skPoint(sketch, "E16.17.15.0", {"position": v(0, -23.71) * mm});
            skArc(sketch, "E16.18.15.0", {"start": v(0, -24.5) * mm, "mid": v(-0.22, -23.94) * mm, "end": v(-0.77, -23.7) * mm});
            skPoint(sketch, "E16.22.15.0", {"position": v(0.96, -27.07) * mm});
            skPoint(sketch, "E16.23.15.0", {"position": v(1.88, -27.02) * mm});
            skLineSegment(sketch, "E16.24.15.0", {"start": v(2.64, -25.1) * mm, "end": v(2.56, -24.36) * mm});
            skArc(sketch, "E16.27.15.0", {"start": v(0, -25.25) * mm, "mid": v(0.02, -25.4) * mm, "end": v(0.06, -25.55) * mm});
            skLineSegment(sketch, "E16.31.15.0", {"start": v(1.76, -27.04) * mm, "end": v(1.42, -27.07) * mm});
            skLineSegment(sketch, "E16.34.15.0", {"start": v(1.08, -27.07) * mm, "end": v(1.42, -27.07) * mm});
            skArc(sketch, "E16.37.15.0", {"start": v(1.76, -27.04) * mm, "mid": v(1.86, -27) * mm, "end": v(1.95, -26.92) * mm});
            skArc(sketch, "E16.41.15.0", {"start": v(0.88, -26.97) * mm, "mid": v(0.97, -27.05) * mm, "end": v(1.08, -27.07) * mm});
            skArc(sketch, "E16.45.15.0", {"start": v(2.61, -25.42) * mm, "mid": v(2.64, -25.26) * mm, "end": v(2.64, -25.1) * mm});
            skArc(sketch, "E16.49.15.0", {"start": v(2.65, -25.26) * mm, "mid": v(2.65, -25.26) * mm, "end": v(2.65, -25.26) * mm});
            skArc(sketch, "E16.53.15.0", {"start": v(2.65, -25.26) * mm, "mid": v(2.65, -25.26) * mm, "end": v(2.65, -25.26) * mm});
            skArc(sketch, "E16.1.16.0", {"start": v(5.37, -24.98) * mm, "mid": v(5.88, -25.63) * mm, "end": v(6.47, -26.2) * mm});
            skPoint(sketch, "E16.4.16.0", {"position": v(5.28, -24.84) * mm});
            skPoint(sketch, "E16.5.16.0", {"position": v(7.85, -24.16) * mm});
            skLineSegment(sketch, "E16.6.16.0", {"start": v(5.25, -24.7) * mm, "end": v(5.1, -23.96) * mm});
            skArc(sketch, "E16.9.16.0", {"start": v(7.84, -24.32) * mm, "mid": v(7.72, -25.13) * mm, "end": v(7.5, -25.92) * mm});
            skArc(sketch, "E16.13.16.0", {"start": v(8.05, -22.3) * mm, "mid": v(7.61, -22.7) * mm, "end": v(7.57, -23.3) * mm});
            skPoint(sketch, "E16.17.16.0", {"position": v(4.93, -23.2) * mm});
            skArc(sketch, "E16.18.16.0", {"start": v(5.1, -23.96) * mm, "mid": v(4.76, -23.46) * mm, "end": v(4.18, -23.34) * mm});
            skPoint(sketch, "E16.22.16.0", {"position": v(6.56, -26.28) * mm});
            skPoint(sketch, "E16.23.16.0", {"position": v(7.46, -26.04) * mm});
            skLineSegment(sketch, "E16.24.16.0", {"start": v(7.8, -24.01) * mm, "end": v(7.57, -23.3) * mm});
            skArc(sketch, "E16.27.16.0", {"start": v(5.25, -24.7) * mm, "mid": v(5.3, -24.84) * mm, "end": v(5.37, -24.98) * mm});
            skLineSegment(sketch, "E16.31.16.0", {"start": v(7.34, -26.08) * mm, "end": v(7.02, -26.19) * mm});
            skLineSegment(sketch, "E16.34.16.0", {"start": v(6.69, -26.26) * mm, "end": v(7.02, -26.19) * mm});
            skArc(sketch, "E16.37.16.0", {"start": v(7.34, -26.08) * mm, "mid": v(7.44, -26.02) * mm, "end": v(7.5, -25.92) * mm});
            skArc(sketch, "E16.41.16.0", {"start": v(6.47, -26.2) * mm, "mid": v(6.57, -26.25) * mm, "end": v(6.69, -26.26) * mm});
            skArc(sketch, "E16.45.16.0", {"start": v(7.84, -24.32) * mm, "mid": v(7.84, -24.16) * mm, "end": v(7.8, -24.01) * mm});
            skArc(sketch, "E16.49.16.0", {"start": v(7.85, -24.16) * mm, "mid": v(7.85, -24.16) * mm, "end": v(7.85, -24.15) * mm});
            skArc(sketch, "E16.53.16.0", {"start": v(7.85, -24.16) * mm, "mid": v(7.85, -24.16) * mm, "end": v(7.85, -24.15) * mm});
            skArc(sketch, "E16.1.17.0", {"start": v(10.45, -23.32) * mm, "mid": v(11.08, -23.84) * mm, "end": v(11.77, -24.28) * mm});
            skPoint(sketch, "E16.4.17.0", {"position": v(10.33, -23.2) * mm});
            skPoint(sketch, "E16.5.17.0", {"position": v(12.7, -22) * mm});
            skLineSegment(sketch, "E16.6.17.0", {"start": v(10.27, -23.06) * mm, "end": v(9.96, -22.37) * mm});
            skArc(sketch, "E16.9.17.0", {"start": v(12.72, -22.16) * mm, "mid": v(12.78, -22.98) * mm, "end": v(12.73, -23.8) * mm});
            skArc(sketch, "E16.13.17.0", {"start": v(12.51, -20.14) * mm, "mid": v(12.16, -20.62) * mm, "end": v(12.25, -21.21) * mm});
            skPoint(sketch, "E16.17.17.0", {"position": v(9.64, -21.66) * mm});
            skArc(sketch, "E16.18.17.0", {"start": v(9.96, -22.37) * mm, "mid": v(9.53, -21.96) * mm, "end": v(8.94, -21.96) * mm});
            skPoint(sketch, "E16.22.17.0", {"position": v(11.88, -24.34) * mm});
            skPoint(sketch, "E16.23.17.0", {"position": v(12.7, -23.92) * mm});
            skLineSegment(sketch, "E16.24.17.0", {"start": v(12.62, -21.87) * mm, "end": v(12.25, -21.21) * mm});
            skArc(sketch, "E16.27.17.0", {"start": v(10.27, -23.06) * mm, "mid": v(10.35, -23.2) * mm, "end": v(10.45, -23.32) * mm});
            skLineSegment(sketch, "E16.31.17.0", {"start": v(12.6, -23.99) * mm, "end": v(12.3, -24.15) * mm});
            skLineSegment(sketch, "E16.34.17.0", {"start": v(12, -24.3) * mm, "end": v(12.3, -24.15) * mm});
            skArc(sketch, "E16.37.17.0", {"start": v(12.6, -23.99) * mm, "mid": v(12.68, -23.9) * mm, "end": v(12.73, -23.8) * mm});
            skArc(sketch, "E16.41.17.0", {"start": v(11.77, -24.28) * mm, "mid": v(11.88, -24.31) * mm, "end": v(12, -24.3) * mm});
            skArc(sketch, "E16.45.17.0", {"start": v(12.72, -22.16) * mm, "mid": v(12.69, -22) * mm, "end": v(12.62, -21.87) * mm});
            skArc(sketch, "E16.49.17.0", {"start": v(12.7, -22) * mm, "mid": v(12.7, -22) * mm, "end": v(12.7, -22) * mm});
            skArc(sketch, "E16.53.17.0", {"start": v(12.7, -22) * mm, "mid": v(12.7, -22) * mm, "end": v(12.7, -22) * mm});
            skArc(sketch, "E16.1.18.0", {"start": v(15.07, -20.64) * mm, "mid": v(15.8, -21.02) * mm, "end": v(16.56, -21.3) * mm});
            skPoint(sketch, "E16.4.18.0", {"position": v(14.93, -20.55) * mm});
            skPoint(sketch, "E16.5.18.0", {"position": v(17, -18.88) * mm});
            skLineSegment(sketch, "E16.6.18.0", {"start": v(14.84, -20.43) * mm, "end": v(14.4, -19.81) * mm});
            skArc(sketch, "E16.9.18.0", {"start": v(17.05, -19.03) * mm, "mid": v(17.28, -19.82) * mm, "end": v(17.4, -20.63) * mm});
            skArc(sketch, "E16.13.18.0", {"start": v(16.43, -17.1) * mm, "mid": v(16.18, -17.64) * mm, "end": v(16.39, -18.2) * mm});
            skPoint(sketch, "E16.17.18.0", {"position": v(13.94, -19.18) * mm});
            skArc(sketch, "E16.18.18.0", {"start": v(14.4, -19.81) * mm, "mid": v(13.9, -19.5) * mm, "end": v(13.3, -19.62) * mm});
            skPoint(sketch, "E16.22.18.0", {"position": v(16.69, -21.34) * mm});
            skPoint(sketch, "E16.23.18.0", {"position": v(17.4, -20.76) * mm});
            skLineSegment(sketch, "E16.24.18.0", {"start": v(16.9, -18.76) * mm, "end": v(16.39, -18.2) * mm});
            skArc(sketch, "E16.27.18.0", {"start": v(14.84, -20.43) * mm, "mid": v(14.94, -20.54) * mm, "end": v(15.07, -20.64) * mm});
            skLineSegment(sketch, "E16.31.18.0", {"start": v(17.31, -20.84) * mm, "end": v(17.06, -21.07) * mm});
            skLineSegment(sketch, "E16.34.18.0", {"start": v(16.79, -21.27) * mm, "end": v(17.06, -21.07) * mm});
            skArc(sketch, "E16.37.18.0", {"start": v(17.31, -20.84) * mm, "mid": v(17.38, -20.75) * mm, "end": v(17.4, -20.63) * mm});
            skArc(sketch, "E16.41.18.0", {"start": v(16.56, -21.3) * mm, "mid": v(16.68, -21.31) * mm, "end": v(16.79, -21.27) * mm});
            skArc(sketch, "E16.45.18.0", {"start": v(17.05, -19.03) * mm, "mid": v(16.99, -18.89) * mm, "end": v(16.9, -18.76) * mm});
            skArc(sketch, "E16.49.18.0", {"start": v(17, -18.88) * mm, "mid": v(17, -18.88) * mm, "end": v(17, -18.87) * mm});
            skArc(sketch, "E16.53.18.0", {"start": v(17, -18.88) * mm, "mid": v(17, -18.88) * mm, "end": v(17, -18.87) * mm});
            skArc(sketch, "E16.1.19.0", {"start": v(19.03, -17.05) * mm, "mid": v(19.82, -17.28) * mm, "end": v(20.63, -17.4) * mm});
            skPoint(sketch, "E16.4.19.0", {"position": v(18.88, -17) * mm});
            skPoint(sketch, "E16.5.19.0", {"position": v(20.55, -14.93) * mm});
            skLineSegment(sketch, "E16.6.19.0", {"start": v(18.76, -16.9) * mm, "end": v(18.2, -16.39) * mm});
            skArc(sketch, "E16.9.19.0", {"start": v(20.64, -15.07) * mm, "mid": v(21.02, -15.8) * mm, "end": v(21.3, -16.56) * mm});
            skArc(sketch, "E16.13.19.0", {"start": v(19.62, -13.3) * mm, "mid": v(19.5, -13.9) * mm, "end": v(19.81, -14.4) * mm});
            skPoint(sketch, "E16.17.19.0", {"position": v(17.62, -15.87) * mm});
            skArc(sketch, "E16.18.19.0", {"start": v(18.2, -16.39) * mm, "mid": v(17.64, -16.18) * mm, "end": v(17.1, -16.43) * mm});
            skPoint(sketch, "E16.22.19.0", {"position": v(20.76, -17.4) * mm});
            skPoint(sketch, "E16.23.19.0", {"position": v(21.34, -16.69) * mm});
            skLineSegment(sketch, "E16.24.19.0", {"start": v(20.43, -14.84) * mm, "end": v(19.81, -14.4) * mm});
            skArc(sketch, "E16.27.19.0", {"start": v(18.76, -16.9) * mm, "mid": v(18.89, -16.99) * mm, "end": v(19.03, -17.05) * mm});
            skLineSegment(sketch, "E16.31.19.0", {"start": v(21.27, -16.79) * mm, "end": v(21.07, -17.06) * mm});
            skLineSegment(sketch, "E16.34.19.0", {"start": v(20.84, -17.31) * mm, "end": v(21.07, -17.06) * mm});
            skArc(sketch, "E16.37.19.0", {"start": v(21.27, -16.79) * mm, "mid": v(21.31, -16.68) * mm, "end": v(21.3, -16.56) * mm});
            skArc(sketch, "E16.41.19.0", {"start": v(20.63, -17.4) * mm, "mid": v(20.75, -17.38) * mm, "end": v(20.84, -17.31) * mm});
            skArc(sketch, "E16.45.19.0", {"start": v(20.64, -15.07) * mm, "mid": v(20.54, -14.94) * mm, "end": v(20.43, -14.84) * mm});
            skArc(sketch, "E16.49.19.0", {"start": v(20.55, -14.93) * mm, "mid": v(20.55, -14.93) * mm, "end": v(20.55, -14.93) * mm});
            skArc(sketch, "E16.53.19.0", {"start": v(20.55, -14.93) * mm, "mid": v(20.55, -14.93) * mm, "end": v(20.55, -14.93) * mm});
            skArc(sketch, "E16.1.20.0", {"start": v(22.16, -12.72) * mm, "mid": v(22.98, -12.78) * mm, "end": v(23.8, -12.73) * mm});
            skPoint(sketch, "E16.4.20.0", {"position": v(22, -12.7) * mm});
            skPoint(sketch, "E16.5.20.0", {"position": v(23.2, -10.33) * mm});
            skLineSegment(sketch, "E16.6.20.0", {"start": v(21.87, -12.62) * mm, "end": v(21.21, -12.25) * mm});
            skArc(sketch, "E16.9.20.0", {"start": v(23.32, -10.45) * mm, "mid": v(23.84, -11.08) * mm, "end": v(24.28, -11.77) * mm});
            skArc(sketch, "E16.13.20.0", {"start": v(21.96, -8.94) * mm, "mid": v(21.96, -9.53) * mm, "end": v(22.37, -9.96) * mm});
            skPoint(sketch, "E16.17.20.0", {"position": v(20.53, -11.86) * mm});
            skArc(sketch, "E16.18.20.0", {"start": v(21.21, -12.25) * mm, "mid": v(20.62, -12.16) * mm, "end": v(20.14, -12.51) * mm});
            skPoint(sketch, "E16.22.20.0", {"position": v(23.92, -12.7) * mm});
            skPoint(sketch, "E16.23.20.0", {"position": v(24.34, -11.88) * mm});
            skLineSegment(sketch, "E16.24.20.0", {"start": v(23.06, -10.27) * mm, "end": v(22.37, -9.96) * mm});
            skArc(sketch, "E16.27.20.0", {"start": v(21.87, -12.62) * mm, "mid": v(22, -12.69) * mm, "end": v(22.16, -12.72) * mm});
            skLineSegment(sketch, "E16.31.20.0", {"start": v(24.3, -12) * mm, "end": v(24.15, -12.3) * mm});
            skLineSegment(sketch, "E16.34.20.0", {"start": v(23.99, -12.6) * mm, "end": v(24.15, -12.3) * mm});
            skArc(sketch, "E16.37.20.0", {"start": v(24.3, -12) * mm, "mid": v(24.31, -11.88) * mm, "end": v(24.28, -11.77) * mm});
            skArc(sketch, "E16.41.20.0", {"start": v(23.8, -12.73) * mm, "mid": v(23.9, -12.68) * mm, "end": v(23.99, -12.6) * mm});
            skArc(sketch, "E16.45.20.0", {"start": v(23.32, -10.45) * mm, "mid": v(23.2, -10.35) * mm, "end": v(23.06, -10.27) * mm});
            skArc(sketch, "E16.49.20.0", {"start": v(23.2, -10.33) * mm, "mid": v(23.2, -10.33) * mm, "end": v(23.2, -10.33) * mm});
            skArc(sketch, "E16.53.20.0", {"start": v(23.2, -10.33) * mm, "mid": v(23.2, -10.33) * mm, "end": v(23.2, -10.33) * mm});
            skArc(sketch, "E16.1.21.0", {"start": v(24.32, -7.84) * mm, "mid": v(25.13, -7.72) * mm, "end": v(25.92, -7.5) * mm});
            skPoint(sketch, "E16.4.21.0", {"position": v(24.16, -7.85) * mm});
            skPoint(sketch, "E16.5.21.0", {"position": v(24.84, -5.28) * mm});
            skLineSegment(sketch, "E16.6.21.0", {"start": v(24.01, -7.8) * mm, "end": v(23.3, -7.57) * mm});
            skArc(sketch, "E16.9.21.0", {"start": v(24.98, -5.37) * mm, "mid": v(25.63, -5.88) * mm, "end": v(26.2, -6.47) * mm});
            skArc(sketch, "E16.13.21.0", {"start": v(23.34, -4.18) * mm, "mid": v(23.46, -4.76) * mm, "end": v(23.96, -5.1) * mm});
            skPoint(sketch, "E16.17.21.0", {"position": v(22.55, -7.33) * mm});
            skArc(sketch, "E16.18.21.0", {"start": v(23.3, -7.57) * mm, "mid": v(22.7, -7.61) * mm, "end": v(22.3, -8.05) * mm});
            skPoint(sketch, "E16.22.21.0", {"position": v(26.04, -7.46) * mm});
            skPoint(sketch, "E16.23.21.0", {"position": v(26.28, -6.56) * mm});
            skLineSegment(sketch, "E16.24.21.0", {"start": v(24.7, -5.25) * mm, "end": v(23.96, -5.1) * mm});
            skArc(sketch, "E16.27.21.0", {"start": v(24.01, -7.8) * mm, "mid": v(24.16, -7.84) * mm, "end": v(24.32, -7.84) * mm});
            skLineSegment(sketch, "E16.31.21.0", {"start": v(26.26, -6.69) * mm, "end": v(26.19, -7.02) * mm});
            skLineSegment(sketch, "E16.34.21.0", {"start": v(26.08, -7.34) * mm, "end": v(26.19, -7.02) * mm});
            skArc(sketch, "E16.37.21.0", {"start": v(26.26, -6.69) * mm, "mid": v(26.25, -6.57) * mm, "end": v(26.2, -6.47) * mm});
            skArc(sketch, "E16.41.21.0", {"start": v(25.92, -7.5) * mm, "mid": v(26.02, -7.44) * mm, "end": v(26.08, -7.34) * mm});
            skArc(sketch, "E16.45.21.0", {"start": v(24.98, -5.37) * mm, "mid": v(24.84, -5.3) * mm, "end": v(24.7, -5.25) * mm});
            skArc(sketch, "E16.49.21.0", {"start": v(24.85, -5.28) * mm, "mid": v(24.84, -5.28) * mm, "end": v(24.84, -5.28) * mm});
            skArc(sketch, "E16.53.21.0", {"start": v(24.85, -5.28) * mm, "mid": v(24.84, -5.28) * mm, "end": v(24.84, -5.28) * mm});
            skArc(sketch, "E16.1.22.0", {"start": v(25.42, -2.61) * mm, "mid": v(26.19, -2.33) * mm, "end": v(26.92, -1.95) * mm});
            skPoint(sketch, "E16.4.22.0", {"position": v(25.26, -2.66) * mm});
            skPoint(sketch, "E16.5.22.0", {"position": v(25.4, 0) * mm});
            skLineSegment(sketch, "E16.6.22.0", {"start": v(25.1, -2.64) * mm, "end": v(24.36, -2.56) * mm});
            skArc(sketch, "E16.9.22.0", {"start": v(25.55, -0.06) * mm, "mid": v(26.29, -0.42) * mm, "end": v(26.97, -0.88) * mm});
            skArc(sketch, "E16.13.22.0", {"start": v(23.7, 0.77) * mm, "mid": v(23.94, 0.22) * mm, "end": v(24.5, 0) * mm});
            skPoint(sketch, "E16.17.22.0", {"position": v(23.58, -2.48) * mm});
            skArc(sketch, "E16.18.22.0", {"start": v(24.36, -2.56) * mm, "mid": v(23.79, -2.72) * mm, "end": v(23.49, -3.24) * mm});
            skPoint(sketch, "E16.22.22.0", {"position": v(27.02, -1.88) * mm});
            skPoint(sketch, "E16.23.22.0", {"position": v(27.07, -0.96) * mm});
            skLineSegment(sketch, "E16.24.22.0", {"start": v(25.25, 0) * mm, "end": v(24.5, 0) * mm});
            skArc(sketch, "E16.27.22.0", {"start": v(25.1, -2.64) * mm, "mid": v(25.26, -2.64) * mm, "end": v(25.42, -2.61) * mm});
            skLineSegment(sketch, "E16.31.22.0", {"start": v(27.07, -1.08) * mm, "end": v(27.07, -1.42) * mm});
            skLineSegment(sketch, "E16.34.22.0", {"start": v(27.04, -1.76) * mm, "end": v(27.07, -1.42) * mm});
            skArc(sketch, "E16.37.22.0", {"start": v(27.07, -1.08) * mm, "mid": v(27.05, -0.97) * mm, "end": v(26.97, -0.88) * mm});
            skArc(sketch, "E16.41.22.0", {"start": v(26.92, -1.95) * mm, "mid": v(27, -1.86) * mm, "end": v(27.04, -1.76) * mm});
            skArc(sketch, "E16.45.22.0", {"start": v(25.55, -0.06) * mm, "mid": v(25.4, -0.02) * mm, "end": v(25.25, 0) * mm});
            skArc(sketch, "E16.49.22.0", {"start": v(25.4, 0) * mm, "mid": v(25.4, 0) * mm, "end": v(25.4, 0) * mm});
            skArc(sketch, "E16.53.22.0", {"start": v(25.4, 0) * mm, "mid": v(25.4, 0) * mm, "end": v(25.4, 0) * mm});
            skArc(sketch, "E16.1.23.0", {"start": v(25.4, 2.73) * mm, "mid": v(26.1, 3.17) * mm, "end": v(26.73, 3.7) * mm});
            skPoint(sketch, "E16.4.23.0", {"position": v(25.26, 2.66) * mm});
            skPoint(sketch, "E16.5.23.0", {"position": v(24.84, 5.28) * mm});
            skLineSegment(sketch, "E16.6.23.0", {"start": v(25.1, 2.64) * mm, "end": v(24.36, 2.56) * mm});
            skArc(sketch, "E16.9.23.0", {"start": v(25, 5.25) * mm, "mid": v(25.8, 5.05) * mm, "end": v(26.57, 4.75) * mm});
            skArc(sketch, "E16.13.23.0", {"start": v(23.02, 5.68) * mm, "mid": v(23.37, 5.2) * mm, "end": v(23.96, 5.1) * mm});
            skPoint(sketch, "E16.17.23.0", {"position": v(23.58, 2.48) * mm});
            skArc(sketch, "E16.18.23.0", {"start": v(24.36, 2.56) * mm, "mid": v(23.83, 2.28) * mm, "end": v(23.65, 1.71) * mm});
            skPoint(sketch, "E16.22.23.0", {"position": v(26.82, 3.78) * mm});
            skPoint(sketch, "E16.23.23.0", {"position": v(26.68, 4.7) * mm});
            skLineSegment(sketch, "E16.24.23.0", {"start": v(24.7, 5.25) * mm, "end": v(23.96, 5.1) * mm});
            skArc(sketch, "E16.27.23.0", {"start": v(25.1, 2.64) * mm, "mid": v(25.26, 2.67) * mm, "end": v(25.4, 2.73) * mm});
            skLineSegment(sketch, "E16.31.23.0", {"start": v(26.7, 4.57) * mm, "end": v(26.78, 4.24) * mm});
            skLineSegment(sketch, "E16.34.23.0", {"start": v(26.81, 3.9) * mm, "end": v(26.78, 4.24) * mm});
            skArc(sketch, "E16.37.23.0", {"start": v(26.7, 4.57) * mm, "mid": v(26.66, 4.68) * mm, "end": v(26.57, 4.75) * mm});
            skArc(sketch, "E16.41.23.0", {"start": v(26.73, 3.7) * mm, "mid": v(26.8, 3.79) * mm, "end": v(26.81, 3.9) * mm});
            skArc(sketch, "E16.45.23.0", {"start": v(25, 5.25) * mm, "mid": v(24.85, 5.27) * mm, "end": v(24.7, 5.25) * mm});
            skArc(sketch, "E16.49.23.0", {"start": v(24.85, 5.28) * mm, "mid": v(24.84, 5.28) * mm, "end": v(24.84, 5.28) * mm});
            skArc(sketch, "E16.53.23.0", {"start": v(24.85, 5.28) * mm, "mid": v(24.84, 5.28) * mm, "end": v(24.84, 5.28) * mm});
            skArc(sketch, "E16.1.24.0", {"start": v(24.28, 7.95) * mm, "mid": v(24.87, 8.53) * mm, "end": v(25.38, 9.17) * mm});
            skPoint(sketch, "E16.4.24.0", {"position": v(24.16, 7.85) * mm});
            skPoint(sketch, "E16.5.24.0", {"position": v(23.2, 10.33) * mm});
            skLineSegment(sketch, "E16.6.24.0", {"start": v(24.01, 7.8) * mm, "end": v(23.3, 7.57) * mm});
            skArc(sketch, "E16.9.24.0", {"start": v(23.37, 10.34) * mm, "mid": v(24.19, 10.3) * mm, "end": v(25, 10.17) * mm});
            skArc(sketch, "E16.13.24.0", {"start": v(21.34, 10.34) * mm, "mid": v(21.78, 9.94) * mm, "end": v(22.37, 9.96) * mm});
            skPoint(sketch, "E16.17.24.0", {"position": v(22.55, 7.33) * mm});
            skArc(sketch, "E16.18.24.0", {"start": v(23.3, 7.57) * mm, "mid": v(22.84, 7.19) * mm, "end": v(22.78, 6.6) * mm});
            skPoint(sketch, "E16.22.24.0", {"position": v(25.45, 9.28) * mm});
            skPoint(sketch, "E16.23.24.0", {"position": v(25.12, 10.14) * mm});
            skLineSegment(sketch, "E16.24.24.0", {"start": v(23.06, 10.27) * mm, "end": v(22.37, 9.96) * mm});
            skArc(sketch, "E16.27.24.0", {"start": v(24.01, 7.8) * mm, "mid": v(24.15, 7.86) * mm, "end": v(24.28, 7.95) * mm});
            skLineSegment(sketch, "E16.31.24.0", {"start": v(25.17, 10.02) * mm, "end": v(25.3, 9.72) * mm});
            skLineSegment(sketch, "E16.34.24.0", {"start": v(25.41, 9.4) * mm, "end": v(25.3, 9.72) * mm});
            skArc(sketch, "E16.37.24.0", {"start": v(25.17, 10.02) * mm, "mid": v(25.1, 10.12) * mm, "end": v(25, 10.17) * mm});
            skArc(sketch, "E16.41.24.0", {"start": v(25.38, 9.17) * mm, "mid": v(25.42, 9.28) * mm, "end": v(25.41, 9.4) * mm});
            skArc(sketch, "E16.45.24.0", {"start": v(23.37, 10.34) * mm, "mid": v(23.21, 10.32) * mm, "end": v(23.06, 10.27) * mm});
            skArc(sketch, "E16.49.24.0", {"start": v(23.2, 10.33) * mm, "mid": v(23.2, 10.33) * mm, "end": v(23.2, 10.33) * mm});
            skArc(sketch, "E16.53.24.0", {"start": v(23.2, 10.33) * mm, "mid": v(23.2, 10.33) * mm, "end": v(23.2, 10.33) * mm});
            skArc(sketch, "E16.1.25.0", {"start": v(22.1, 12.83) * mm, "mid": v(22.55, 13.51) * mm, "end": v(22.92, 14.25) * mm});
            skPoint(sketch, "E16.4.25.0", {"position": v(22, 12.7) * mm});
            skPoint(sketch, "E16.5.25.0", {"position": v(20.55, 14.93) * mm});
            skLineSegment(sketch, "E16.6.25.0", {"start": v(21.87, 12.62) * mm, "end": v(21.21, 12.25) * mm});
            skArc(sketch, "E16.9.25.0", {"start": v(20.7, 14.97) * mm, "mid": v(21.52, 15.1) * mm, "end": v(22.34, 15.14) * mm});
            skArc(sketch, "E16.13.25.0", {"start": v(18.72, 14.55) * mm, "mid": v(19.24, 14.25) * mm, "end": v(19.81, 14.4) * mm});
            skPoint(sketch, "E16.17.25.0", {"position": v(20.53, 11.86) * mm});
            skArc(sketch, "E16.18.25.0", {"start": v(21.21, 12.25) * mm, "mid": v(20.84, 11.78) * mm, "end": v(20.9, 11.18) * mm});
            skPoint(sketch, "E16.22.25.0", {"position": v(22.97, 14.36) * mm});
            skPoint(sketch, "E16.23.25.0", {"position": v(22.46, 15.14) * mm});
            skLineSegment(sketch, "E16.24.25.0", {"start": v(20.43, 14.84) * mm, "end": v(19.81, 14.4) * mm});
            skArc(sketch, "E16.27.25.0", {"start": v(21.87, 12.62) * mm, "mid": v(22, 12.71) * mm, "end": v(22.1, 12.83) * mm});
            skLineSegment(sketch, "E16.31.25.0", {"start": v(22.54, 15.04) * mm, "end": v(22.74, 14.76) * mm});
            skLineSegment(sketch, "E16.34.25.0", {"start": v(22.9, 14.47) * mm, "end": v(22.74, 14.76) * mm});
            skArc(sketch, "E16.37.25.0", {"start": v(22.54, 15.04) * mm, "mid": v(22.45, 15.11) * mm, "end": v(22.34, 15.14) * mm});
            skArc(sketch, "E16.41.25.0", {"start": v(22.92, 14.25) * mm, "mid": v(22.94, 14.36) * mm, "end": v(22.9, 14.47) * mm});
            skArc(sketch, "E16.45.25.0", {"start": v(20.7, 14.97) * mm, "mid": v(20.56, 14.92) * mm, "end": v(20.43, 14.84) * mm});
            skArc(sketch, "E16.49.25.0", {"start": v(20.55, 14.93) * mm, "mid": v(20.55, 14.93) * mm, "end": v(20.55, 14.93) * mm});
            skArc(sketch, "E16.53.25.0", {"start": v(20.55, 14.93) * mm, "mid": v(20.55, 14.93) * mm, "end": v(20.55, 14.93) * mm});
            skArc(sketch, "E16.1.26.0", {"start": v(18.95, 17.14) * mm, "mid": v(19.25, 17.9) * mm, "end": v(19.46, 18.7) * mm});
            skPoint(sketch, "E16.4.26.0", {"position": v(18.88, 17) * mm});
            skPoint(sketch, "E16.5.26.0", {"position": v(17, 18.88) * mm});
            skLineSegment(sketch, "E16.6.26.0", {"start": v(18.76, 16.9) * mm, "end": v(18.2, 16.39) * mm});
            skArc(sketch, "E16.9.26.0", {"start": v(17.14, 18.95) * mm, "mid": v(17.9, 19.25) * mm, "end": v(18.7, 19.46) * mm});
            skArc(sketch, "E16.13.26.0", {"start": v(15.29, 18.13) * mm, "mid": v(15.85, 17.94) * mm, "end": v(16.39, 18.2) * mm});
            skPoint(sketch, "E16.17.26.0", {"position": v(17.62, 15.87) * mm});
            skArc(sketch, "E16.18.26.0", {"start": v(18.2, 16.39) * mm, "mid": v(17.94, 15.85) * mm, "end": v(18.13, 15.29) * mm});
            skPoint(sketch, "E16.22.26.0", {"position": v(19.48, 18.83) * mm});
            skPoint(sketch, "E16.23.26.0", {"position": v(18.83, 19.48) * mm});
            skLineSegment(sketch, "E16.24.26.0", {"start": v(16.9, 18.76) * mm, "end": v(16.39, 18.2) * mm});
            skArc(sketch, "E16.27.26.0", {"start": v(18.76, 16.9) * mm, "mid": v(18.87, 17) * mm, "end": v(18.95, 17.14) * mm});
            skLineSegment(sketch, "E16.31.26.0", {"start": v(18.92, 19.4) * mm, "end": v(19.17, 19.17) * mm});
            skLineSegment(sketch, "E16.34.26.0", {"start": v(19.4, 18.92) * mm, "end": v(19.17, 19.17) * mm});
            skArc(sketch, "E16.37.26.0", {"start": v(18.92, 19.4) * mm, "mid": v(18.82, 19.45) * mm, "end": v(18.7, 19.46) * mm});
            skArc(sketch, "E16.41.26.0", {"start": v(19.46, 18.7) * mm, "mid": v(19.45, 18.82) * mm, "end": v(19.4, 18.92) * mm});
            skArc(sketch, "E16.45.26.0", {"start": v(17.14, 18.95) * mm, "mid": v(17, 18.87) * mm, "end": v(16.9, 18.76) * mm});
            skArc(sketch, "E16.49.26.0", {"start": v(17, 18.88) * mm, "mid": v(17, 18.88) * mm, "end": v(17, 18.87) * mm});
            skArc(sketch, "E16.53.26.0", {"start": v(17, 18.88) * mm, "mid": v(17, 18.88) * mm, "end": v(17, 18.87) * mm});
            skArc(sketch, "E16.1.27.0", {"start": v(14.97, 20.7) * mm, "mid": v(15.1, 21.52) * mm, "end": v(15.14, 22.34) * mm});
            skPoint(sketch, "E16.4.27.0", {"position": v(14.93, 20.55) * mm});
            skPoint(sketch, "E16.5.27.0", {"position": v(12.7, 22) * mm});
            skLineSegment(sketch, "E16.6.27.0", {"start": v(14.84, 20.43) * mm, "end": v(14.4, 19.81) * mm});
            skArc(sketch, "E16.9.27.0", {"start": v(12.83, 22.1) * mm, "mid": v(13.51, 22.55) * mm, "end": v(14.25, 22.92) * mm});
            skArc(sketch, "E16.13.27.0", {"start": v(11.18, 20.9) * mm, "mid": v(11.78, 20.84) * mm, "end": v(12.25, 21.21) * mm});
            skPoint(sketch, "E16.17.27.0", {"position": v(13.94, 19.18) * mm});
            skArc(sketch, "E16.18.27.0", {"start": v(14.4, 19.81) * mm, "mid": v(14.25, 19.24) * mm, "end": v(14.55, 18.72) * mm});
            skPoint(sketch, "E16.22.27.0", {"position": v(15.14, 22.46) * mm});
            skPoint(sketch, "E16.23.27.0", {"position": v(14.36, 22.97) * mm});
            skLineSegment(sketch, "E16.24.27.0", {"start": v(12.62, 21.87) * mm, "end": v(12.25, 21.21) * mm});
            skArc(sketch, "E16.27.27.0", {"start": v(14.84, 20.43) * mm, "mid": v(14.92, 20.56) * mm, "end": v(14.97, 20.7) * mm});
            skLineSegment(sketch, "E16.31.27.0", {"start": v(14.47, 22.9) * mm, "end": v(14.76, 22.74) * mm});
            skLineSegment(sketch, "E16.34.27.0", {"start": v(15.04, 22.54) * mm, "end": v(14.76, 22.74) * mm});
            skArc(sketch, "E16.37.27.0", {"start": v(14.47, 22.9) * mm, "mid": v(14.36, 22.94) * mm, "end": v(14.25, 22.92) * mm});
            skArc(sketch, "E16.41.27.0", {"start": v(15.14, 22.34) * mm, "mid": v(15.11, 22.45) * mm, "end": v(15.04, 22.54) * mm});
            skArc(sketch, "E16.45.27.0", {"start": v(12.83, 22.1) * mm, "mid": v(12.71, 22) * mm, "end": v(12.62, 21.87) * mm});
            skArc(sketch, "E16.49.27.0", {"start": v(12.7, 22) * mm, "mid": v(12.7, 22) * mm, "end": v(12.7, 22) * mm});
            skArc(sketch, "E16.53.27.0", {"start": v(12.7, 22) * mm, "mid": v(12.7, 22) * mm, "end": v(12.7, 22) * mm});
            skArc(sketch, "E16.1.28.0", {"start": v(10.34, 23.37) * mm, "mid": v(10.3, 24.19) * mm, "end": v(10.17, 25) * mm});
            skPoint(sketch, "E16.4.28.0", {"position": v(10.33, 23.2) * mm});
            skPoint(sketch, "E16.5.28.0", {"position": v(7.85, 24.16) * mm});
            skLineSegment(sketch, "E16.6.28.0", {"start": v(10.27, 23.06) * mm, "end": v(9.96, 22.37) * mm});
            skArc(sketch, "E16.9.28.0", {"start": v(7.95, 24.28) * mm, "mid": v(8.53, 24.87) * mm, "end": v(9.17, 25.38) * mm});
            skArc(sketch, "E16.13.28.0", {"start": v(6.6, 22.78) * mm, "mid": v(7.19, 22.84) * mm, "end": v(7.57, 23.3) * mm});
            skPoint(sketch, "E16.17.28.0", {"position": v(9.64, 21.66) * mm});
            skArc(sketch, "E16.18.28.0", {"start": v(9.96, 22.37) * mm, "mid": v(9.94, 21.78) * mm, "end": v(10.34, 21.34) * mm});
            skPoint(sketch, "E16.22.28.0", {"position": v(10.14, 25.12) * mm});
            skPoint(sketch, "E16.23.28.0", {"position": v(9.28, 25.45) * mm});
            skLineSegment(sketch, "E16.24.28.0", {"start": v(7.8, 24.01) * mm, "end": v(7.57, 23.3) * mm});
            skArc(sketch, "E16.27.28.0", {"start": v(10.27, 23.06) * mm, "mid": v(10.32, 23.21) * mm, "end": v(10.34, 23.37) * mm});
            skLineSegment(sketch, "E16.31.28.0", {"start": v(9.4, 25.41) * mm, "end": v(9.72, 25.3) * mm});
            skLineSegment(sketch, "E16.34.28.0", {"start": v(10.02, 25.17) * mm, "end": v(9.72, 25.3) * mm});
            skArc(sketch, "E16.37.28.0", {"start": v(9.4, 25.41) * mm, "mid": v(9.28, 25.42) * mm, "end": v(9.17, 25.38) * mm});
            skArc(sketch, "E16.41.28.0", {"start": v(10.17, 25) * mm, "mid": v(10.12, 25.1) * mm, "end": v(10.02, 25.17) * mm});
            skArc(sketch, "E16.45.28.0", {"start": v(7.95, 24.28) * mm, "mid": v(7.86, 24.15) * mm, "end": v(7.8, 24.01) * mm});
            skArc(sketch, "E16.49.28.0", {"start": v(7.85, 24.16) * mm, "mid": v(7.85, 24.16) * mm, "end": v(7.85, 24.15) * mm});
            skArc(sketch, "E16.53.28.0", {"start": v(7.85, 24.16) * mm, "mid": v(7.85, 24.16) * mm, "end": v(7.85, 24.15) * mm});
            skArc(sketch, "E16.1.29.0", {"start": v(5.25, 25) * mm, "mid": v(5.05, 25.8) * mm, "end": v(4.75, 26.57) * mm});
            skPoint(sketch, "E16.4.29.0", {"position": v(5.28, 24.84) * mm});
            skPoint(sketch, "E16.5.29.0", {"position": v(2.66, 25.26) * mm});
            skLineSegment(sketch, "E16.6.29.0", {"start": v(5.25, 24.7) * mm, "end": v(5.1, 23.96) * mm});
            skArc(sketch, "E16.9.29.0", {"start": v(2.73, 25.4) * mm, "mid": v(3.17, 26.1) * mm, "end": v(3.7, 26.73) * mm});
            skArc(sketch, "E16.13.29.0", {"start": v(1.71, 23.65) * mm, "mid": v(2.28, 23.83) * mm, "end": v(2.56, 24.36) * mm});
            skPoint(sketch, "E16.17.29.0", {"position": v(4.93, 23.2) * mm});
            skArc(sketch, "E16.18.29.0", {"start": v(5.1, 23.96) * mm, "mid": v(5.2, 23.37) * mm, "end": v(5.68, 23.02) * mm});
            skPoint(sketch, "E16.22.29.0", {"position": v(4.7, 26.68) * mm});
            skPoint(sketch, "E16.23.29.0", {"position": v(3.78, 26.82) * mm});
            skLineSegment(sketch, "E16.24.29.0", {"start": v(2.64, 25.1) * mm, "end": v(2.56, 24.36) * mm});
            skArc(sketch, "E16.27.29.0", {"start": v(5.25, 24.7) * mm, "mid": v(5.27, 24.85) * mm, "end": v(5.25, 25) * mm});
            skLineSegment(sketch, "E16.31.29.0", {"start": v(3.9, 26.81) * mm, "end": v(4.24, 26.78) * mm});
            skLineSegment(sketch, "E16.34.29.0", {"start": v(4.57, 26.7) * mm, "end": v(4.24, 26.78) * mm});
            skArc(sketch, "E16.37.29.0", {"start": v(3.9, 26.81) * mm, "mid": v(3.79, 26.8) * mm, "end": v(3.7, 26.73) * mm});
            skArc(sketch, "E16.41.29.0", {"start": v(4.75, 26.57) * mm, "mid": v(4.68, 26.66) * mm, "end": v(4.57, 26.7) * mm});
            skArc(sketch, "E16.45.29.0", {"start": v(2.73, 25.4) * mm, "mid": v(2.67, 25.26) * mm, "end": v(2.64, 25.1) * mm});
            skArc(sketch, "E16.49.29.0", {"start": v(2.66, 25.26) * mm, "mid": v(2.66, 25.26) * mm, "end": v(2.65, 25.26) * mm});
            skArc(sketch, "E16.53.29.0", {"start": v(2.66, 25.26) * mm, "mid": v(2.66, 25.26) * mm, "end": v(2.65, 25.26) * mm});
            skArc(sketch, "E17.trimOffspring", {"start": v(-16.43, 17.1) * mm, "mid": v(-17.04, 16.5) * mm, "end": v(-17.62, 15.87) * mm});
            skArc(sketch, "E18.trimOffspring", {"start": v(-12.51, 20.14) * mm, "mid": v(-13.23, 19.67) * mm, "end": v(-13.94, 19.18) * mm});
            skArc(sketch, "E19.trimOffspring", {"start": v(-8.05, 22.3) * mm, "mid": v(-8.85, 22) * mm, "end": v(-9.64, 21.66) * mm});
            skArc(sketch, "E20.trimOffspring", {"start": v(1.71, 23.65) * mm, "mid": v(1.24, 23.68) * mm, "end": v(0.77, 23.7) * mm});
            skArc(sketch, "E21.trimOffspring", {"start": v(6.6, 22.78) * mm, "mid": v(5.77, 23) * mm, "end": v(4.93, 23.2) * mm});
            skArc(sketch, "E22.trimOffspring", {"start": v(11.18, 20.9) * mm, "mid": v(10.42, 21.3) * mm, "end": v(9.64, 21.66) * mm});
            skArc(sketch, "E23.trimOffspring", {"start": v(15.29, 18.13) * mm, "mid": v(14.62, 18.67) * mm, "end": v(13.94, 19.18) * mm});
            skArc(sketch, "E24.trimOffspring", {"start": v(18.72, 14.55) * mm, "mid": v(18.18, 15.22) * mm, "end": v(17.62, 15.87) * mm});
            skArc(sketch, "E25.trimOffspring", {"start": v(21.34, 10.34) * mm, "mid": v(20.95, 11.1) * mm, "end": v(20.53, 11.86) * mm});
            skArc(sketch, "E26.trimOffspring", {"start": v(23.02, 5.68) * mm, "mid": v(22.8, 6.5) * mm, "end": v(22.55, 7.33) * mm});
            skArc(sketch, "E27.trimOffspring", {"start": v(23.7, 0.77) * mm, "mid": v(23.66, 1.62) * mm, "end": v(23.58, 2.48) * mm});
            skArc(sketch, "E28.trimOffspring", {"start": v(23.34, -4.18) * mm, "mid": v(23.48, -3.33) * mm, "end": v(23.58, -2.48) * mm});
            skArc(sketch, "E29.trimOffspring", {"start": v(21.96, -8.94) * mm, "mid": v(22.27, -8.14) * mm, "end": v(22.55, -7.33) * mm});
            skArc(sketch, "E30.trimOffspring", {"start": v(19.62, -13.3) * mm, "mid": v(20.1, -12.6) * mm, "end": v(20.53, -11.86) * mm});
            skArc(sketch, "E31.trimOffspring", {"start": v(16.43, -17.1) * mm, "mid": v(17.04, -16.5) * mm, "end": v(17.62, -15.87) * mm});
            skArc(sketch, "E32.trimOffspring", {"start": v(12.51, -20.14) * mm, "mid": v(13.23, -19.67) * mm, "end": v(13.94, -19.18) * mm});
            skArc(sketch, "E33.trimOffspring", {"start": v(8.05, -22.3) * mm, "mid": v(8.85, -22) * mm, "end": v(9.64, -21.66) * mm});
            skArc(sketch, "E34.trimOffspring", {"start": v(3.24, -23.49) * mm, "mid": v(4.09, -23.36) * mm, "end": v(4.93, -23.2) * mm});
            skArc(sketch, "E35.trimOffspring", {"start": v(-1.71, -23.65) * mm, "mid": v(-0.86, -23.7) * mm, "end": v(0, -23.71) * mm});
            skArc(sketch, "E36.trimOffspring", {"start": v(-6.6, -22.78) * mm, "mid": v(-5.77, -23) * mm, "end": v(-4.93, -23.2) * mm});
            skArc(sketch, "E37.trimOffspring", {"start": v(-11.18, -20.9) * mm, "mid": v(-10.42, -21.3) * mm, "end": v(-9.64, -21.66) * mm});
            skArc(sketch, "E38.trimOffspring", {"start": v(-15.29, -18.13) * mm, "mid": v(-14.62, -18.67) * mm, "end": v(-13.94, -19.18) * mm});
            skArc(sketch, "E39.trimOffspring", {"start": v(-18.72, -14.55) * mm, "mid": v(-18.18, -15.22) * mm, "end": v(-17.62, -15.87) * mm});
            skArc(sketch, "E40.trimOffspring", {"start": v(-21.34, -10.34) * mm, "mid": v(-20.95, -11.1) * mm, "end": v(-20.53, -11.86) * mm});
            skArc(sketch, "E41.trimOffspring", {"start": v(-23.02, -5.68) * mm, "mid": v(-22.8, -6.5) * mm, "end": v(-22.55, -7.33) * mm});
            skArc(sketch, "E42.trimOffspring", {"start": v(-23.7, -0.77) * mm, "mid": v(-23.66, -1.62) * mm, "end": v(-23.58, -2.48) * mm});
            skArc(sketch, "E43.trimOffspring", {"start": v(-23.34, 4.18) * mm, "mid": v(-23.48, 3.33) * mm, "end": v(-23.58, 2.48) * mm});
            skArc(sketch, "E44.trimOffspring", {"start": v(-21.96, 8.94) * mm, "mid": v(-22.27, 8.14) * mm, "end": v(-22.55, 7.33) * mm});
            skArc(sketch, "E45.trimOffspring", {"start": v(-19.62, 13.3) * mm, "mid": v(-20.1, 12.6) * mm, "end": v(-20.53, 11.86) * mm});
            skSolve(sketch);
        }
        {
            var Q0;
            Q0=makeQuery(id+"F0.imprint","IMPRINT",FACE,{"disambiguationData":[TD([[makeQuery(id+"F0.imprint","IMPRINT",EDGE,{"derivedFrom":sQuery(id+"F0.wireOp",EDGE,"E1.trimOffspring")}),1.0]])]});
            cPlane(context, id + "F1", {"entities" : qUnion([Q0]), "cplaneType" : CPlaneType.OFFSET, "offset" : 22 * mm, "width" : 152.4 * mm, "height" : 152.4 * mm});
        }
        {
            var Q0;
            Q0=qCreatedBy(id+"F1.planeOp",FACE);
            var sketch = newSketch(context, id + "F2", { "sketchPlane" : qUnion([Q0])});
            skArc(sketch, "E46", {"start": v(-4.49, 35.28) * mm, "mid": v(-5.56, 35.12) * mm, "end": v(-6.63, 34.94) * mm});
            skArc(sketch, "E47.trimOffspring", {"start": v(-0.06, 38.25) * mm, "mid": v(-0.63, 39.42) * mm, "end": v(-1.36, 40.5) * mm});
            skLineSegment(sketch, "E48", {"start": v(-1.57, 40.6) * mm, "end": v(-2.13, 40.58) * mm});
            skLineSegment(sketch, "E49", {"start": v(0, 37.95) * mm, "end": v(0, 36.35) * mm});
            skLineSegment(sketch, "E50.MirrorCS", {"start": v(-2.68, 40.55) * mm, "end": v(-2.13, 40.58) * mm});
            skArc(sketch, "E51.MirrorCS", {"start": v(-3.94, 38.04) * mm, "mid": v(-3.5, 39.27) * mm, "end": v(-2.89, 40.43) * mm});
            skLineSegment(sketch, "E52.MirrorCS", {"start": v(-3.97, 37.74) * mm, "end": v(-3.8, 36.15) * mm});
            skPoint(sketch, "E53.orphan", {"position": v(-3.45, 32.82) * mm});
            skPoint(sketch, "E54.orphan", {"position": v(0, 33) * mm});
            skPoint(sketch, "E55.visualSharp", {"position": v(-3.72, 35.37) * mm});
            skArc(sketch, "E55.filletArc", {"start": v(-3.97, 35.34) * mm, "mid": v(-3.8, 35.43) * mm, "end": v(-3.74, 35.62) * mm});
            skArc(sketch, "E56.filletArc", {"start": v(-4.49, 35.28) * mm, "mid": v(-3.97, 35.57) * mm, "end": v(-3.8, 36.15) * mm});
            skPoint(sketch, "E57.visualSharp", {"position": v(0, 35.56) * mm});
            skArc(sketch, "E57.filletArc", {"start": v(0, 36.35) * mm, "mid": v(0.23, 35.79) * mm, "end": v(0.78, 35.55) * mm});
            skPoint(sketch, "E58.visualSharp", {"position": v(0, 38.1) * mm});
            skArc(sketch, "E58.filletArc", {"start": v(0, 37.95) * mm, "mid": v(-0.01, 38.1) * mm, "end": v(-0.06, 38.25) * mm});
            skPoint(sketch, "E59.visualSharp", {"position": v(-3.98, 37.9) * mm});
            skArc(sketch, "E59.filletArc", {"start": v(-3.94, 38.04) * mm, "mid": v(-3.97, 37.9) * mm, "end": v(-3.97, 37.74) * mm});
            skPoint(sketch, "E60.visualSharp", {"position": v(-2.81, 40.54) * mm});
            skArc(sketch, "E60.filletArc", {"start": v(-2.68, 40.55) * mm, "mid": v(-2.8, 40.51) * mm, "end": v(-2.89, 40.43) * mm});
            skPoint(sketch, "E61.visualSharp", {"position": v(-1.44, 40.61) * mm});
            skArc(sketch, "E61.filletArc", {"start": v(-1.36, 40.5) * mm, "mid": v(-1.45, 40.58) * mm, "end": v(-1.57, 40.6) * mm});
            skArc(sketch, "E62.1.0", {"start": v(-7.56, 35.55) * mm, "mid": v(-7.22, 35.05) * mm, "end": v(-6.63, 34.94) * mm});
            skArc(sketch, "E62.1.1", {"start": v(-11.72, 33.57) * mm, "mid": v(-11.28, 33.97) * mm, "end": v(-11.23, 34.57) * mm});
            skPoint(sketch, "E62.1.2", {"position": v(-7.92, 37.27) * mm});
            skArc(sketch, "E62.1.3", {"start": v(-8, 37.4) * mm, "mid": v(-8.81, 38.43) * mm, "end": v(-9.75, 39.34) * mm});
            skPoint(sketch, "E62.1.4", {"position": v(-9.85, 39.43) * mm});
            skPoint(sketch, "E62.1.5", {"position": v(-11.18, 39.07) * mm});
            skArc(sketch, "E62.1.6", {"start": v(-11.76, 36.4) * mm, "mid": v(-11.58, 37.69) * mm, "end": v(-11.23, 38.95) * mm});
            skLineSegment(sketch, "E62.1.7", {"start": v(-11.73, 36.1) * mm, "end": v(-11.23, 34.57) * mm});
            skLineSegment(sketch, "E62.1.8", {"start": v(-7.9, 37.12) * mm, "end": v(-7.56, 35.55) * mm});
            skPoint(sketch, "E62.1.9", {"position": v(-11.77, 36.24) * mm});
            skArc(sketch, "E62.1.10", {"start": v(-11.05, 39.1) * mm, "mid": v(-11.16, 39.05) * mm, "end": v(-11.23, 38.95) * mm});
            skArc(sketch, "E62.1.11", {"start": v(-11.76, 36.4) * mm, "mid": v(-11.76, 36.24) * mm, "end": v(-11.73, 36.1) * mm});
            skLineSegment(sketch, "E62.1.12", {"start": v(-9.98, 39.4) * mm, "end": v(-10.52, 39.25) * mm});
            skArc(sketch, "E62.1.13", {"start": v(-7.9, 37.12) * mm, "mid": v(-7.94, 37.27) * mm, "end": v(-8, 37.4) * mm});
            skArc(sketch, "E62.1.14", {"start": v(-9.75, 39.34) * mm, "mid": v(-9.86, 39.4) * mm, "end": v(-9.98, 39.4) * mm});
            skLineSegment(sketch, "E62.1.15", {"start": v(-11.05, 39.1) * mm, "end": v(-10.52, 39.25) * mm});
            skArc(sketch, "E62.2.0", {"start": v(-14.78, 33.2) * mm, "mid": v(-14.35, 32.79) * mm, "end": v(-13.75, 32.8) * mm});
            skArc(sketch, "E62.2.1", {"start": v(-18.45, 30.4) * mm, "mid": v(-18.1, 30.88) * mm, "end": v(-18.17, 31.48) * mm});
            skPoint(sketch, "E62.2.2", {"position": v(-15.5, 34.8) * mm});
            skArc(sketch, "E62.2.3", {"start": v(-15.6, 34.92) * mm, "mid": v(-16.6, 35.76) * mm, "end": v(-17.72, 36.46) * mm});
            skPoint(sketch, "E62.2.4", {"position": v(-17.83, 36.52) * mm});
            skPoint(sketch, "E62.2.5", {"position": v(-19.06, 35.9) * mm});
            skArc(sketch, "E62.2.6", {"start": v(-19.07, 33.15) * mm, "mid": v(-19.17, 34.46) * mm, "end": v(-19.08, 35.76) * mm});
            skLineSegment(sketch, "E62.2.7", {"start": v(-18.97, 32.87) * mm, "end": v(-18.17, 31.48) * mm});
            skLineSegment(sketch, "E62.2.8", {"start": v(-15.44, 34.67) * mm, "end": v(-14.78, 33.2) * mm});
            skPoint(sketch, "E62.2.9", {"position": v(-19.05, 33) * mm});
            skArc(sketch, "E62.2.10", {"start": v(-18.94, 35.95) * mm, "mid": v(-19.04, 35.87) * mm, "end": v(-19.08, 35.76) * mm});
            skArc(sketch, "E62.2.11", {"start": v(-19.07, 33.15) * mm, "mid": v(-19.04, 33) * mm, "end": v(-18.97, 32.87) * mm});
            skLineSegment(sketch, "E62.2.12", {"start": v(-17.95, 36.46) * mm, "end": v(-18.45, 36.2) * mm});
            skArc(sketch, "E62.2.13", {"start": v(-15.44, 34.67) * mm, "mid": v(-15.51, 34.8) * mm, "end": v(-15.6, 34.92) * mm});
            skArc(sketch, "E62.2.14", {"start": v(-17.72, 36.46) * mm, "mid": v(-17.83, 36.49) * mm, "end": v(-17.95, 36.46) * mm});
            skLineSegment(sketch, "E62.2.15", {"start": v(-18.94, 35.95) * mm, "end": v(-18.45, 36.2) * mm});
            skArc(sketch, "E63.3.3.0", {"start": v(-21.36, 29.4) * mm, "mid": v(-20.85, 29.09) * mm, "end": v(-20.27, 29.22) * mm});
            skArc(sketch, "E63.4.3.0", {"start": v(-24.37, 25.9) * mm, "mid": v(-24.12, 26.45) * mm, "end": v(-24.32, 27) * mm});
            skPoint(sketch, "E63.8.3.0", {"position": v(-22.4, 30.82) * mm});
            skArc(sketch, "E63.9.3.0", {"start": v(-22.53, 30.9) * mm, "mid": v(-23.68, 31.52) * mm, "end": v(-24.9, 31.98) * mm});
            skPoint(sketch, "E63.13.3.0", {"position": v(-25.04, 32.01) * mm});
            skPoint(sketch, "E63.14.3.0", {"position": v(-26.1, 31.15) * mm});
            skArc(sketch, "E63.15.3.0", {"start": v(-25.55, 28.46) * mm, "mid": v(-25.91, 29.72) * mm, "end": v(-26.1, 31.01) * mm});
            skLineSegment(sketch, "E63.19.3.0", {"start": v(-25.4, 28.2) * mm, "end": v(-24.32, 27) * mm});
            skLineSegment(sketch, "E63.22.3.0", {"start": v(-22.3, 30.7) * mm, "end": v(-21.36, 29.4) * mm});
            skPoint(sketch, "E63.25.3.0", {"position": v(-25.5, 28.31) * mm});
            skArc(sketch, "E63.26.3.0", {"start": v(-26, 31.23) * mm, "mid": v(-26.08, 31.13) * mm, "end": v(-26.1, 31.01) * mm});
            skArc(sketch, "E63.30.3.0", {"start": v(-25.55, 28.46) * mm, "mid": v(-25.48, 28.32) * mm, "end": v(-25.4, 28.2) * mm});
            skLineSegment(sketch, "E63.34.3.0", {"start": v(-25.14, 31.93) * mm, "end": v(-25.57, 31.58) * mm});
            skArc(sketch, "E63.37.3.0", {"start": v(-22.3, 30.7) * mm, "mid": v(-22.4, 30.82) * mm, "end": v(-22.53, 30.9) * mm});
            skArc(sketch, "E63.41.3.0", {"start": v(-24.9, 31.98) * mm, "mid": v(-25.03, 31.98) * mm, "end": v(-25.14, 31.93) * mm});
            skLineSegment(sketch, "E63.45.3.0", {"start": v(-26, 31.23) * mm, "end": v(-25.57, 31.58) * mm});
            skArc(sketch, "E63.3.4.0", {"start": v(-27, 24.32) * mm, "mid": v(-26.45, 24.12) * mm, "end": v(-25.9, 24.37) * mm});
            skArc(sketch, "E63.4.4.0", {"start": v(-29.22, 20.27) * mm, "mid": v(-29.09, 20.85) * mm, "end": v(-29.4, 21.36) * mm});
            skPoint(sketch, "E63.8.4.0", {"position": v(-28.31, 25.5) * mm});
            skArc(sketch, "E63.9.4.0", {"start": v(-28.46, 25.55) * mm, "mid": v(-29.72, 25.91) * mm, "end": v(-31.01, 26.1) * mm});
            skPoint(sketch, "E63.13.4.0", {"position": v(-31.15, 26.1) * mm});
            skPoint(sketch, "E63.14.4.0", {"position": v(-32.01, 25.04) * mm});
            skArc(sketch, "E63.15.4.0", {"start": v(-30.9, 22.53) * mm, "mid": v(-31.52, 23.68) * mm, "end": v(-31.98, 24.9) * mm});
            skLineSegment(sketch, "E63.19.4.0", {"start": v(-30.7, 22.3) * mm, "end": v(-29.4, 21.36) * mm});
            skLineSegment(sketch, "E63.22.4.0", {"start": v(-28.2, 25.4) * mm, "end": v(-27, 24.32) * mm});
            skPoint(sketch, "E63.25.4.0", {"position": v(-30.82, 22.4) * mm});
            skArc(sketch, "E63.26.4.0", {"start": v(-31.93, 25.14) * mm, "mid": v(-31.98, 25.03) * mm, "end": v(-31.98, 24.9) * mm});
            skArc(sketch, "E63.30.4.0", {"start": v(-30.9, 22.53) * mm, "mid": v(-30.82, 22.4) * mm, "end": v(-30.7, 22.3) * mm});
            skLineSegment(sketch, "E63.34.4.0", {"start": v(-31.23, 26) * mm, "end": v(-31.58, 25.57) * mm});
            skArc(sketch, "E63.37.4.0", {"start": v(-28.2, 25.4) * mm, "mid": v(-28.32, 25.48) * mm, "end": v(-28.46, 25.55) * mm});
            skArc(sketch, "E63.41.4.0", {"start": v(-31.01, 26.1) * mm, "mid": v(-31.13, 26.08) * mm, "end": v(-31.23, 26) * mm});
            skLineSegment(sketch, "E63.45.4.0", {"start": v(-31.93, 25.14) * mm, "end": v(-31.58, 25.57) * mm});
            skArc(sketch, "E63.3.5.0", {"start": v(-31.48, 18.17) * mm, "mid": v(-30.88, 18.1) * mm, "end": v(-30.4, 18.45) * mm});
            skArc(sketch, "E63.4.5.0", {"start": v(-32.8, 13.75) * mm, "mid": v(-32.79, 14.35) * mm, "end": v(-33.2, 14.78) * mm});
            skPoint(sketch, "E63.8.5.0", {"position": v(-33, 19.05) * mm});
            skArc(sketch, "E63.9.5.0", {"start": v(-33.15, 19.07) * mm, "mid": v(-34.46, 19.17) * mm, "end": v(-35.76, 19.08) * mm});
            skPoint(sketch, "E63.13.5.0", {"position": v(-35.9, 19.06) * mm});
            skPoint(sketch, "E63.14.5.0", {"position": v(-36.52, 17.83) * mm});
            skArc(sketch, "E63.15.5.0", {"start": v(-34.92, 15.6) * mm, "mid": v(-35.76, 16.6) * mm, "end": v(-36.46, 17.72) * mm});
            skLineSegment(sketch, "E63.19.5.0", {"start": v(-34.67, 15.44) * mm, "end": v(-33.2, 14.78) * mm});
            skLineSegment(sketch, "E63.22.5.0", {"start": v(-32.87, 18.97) * mm, "end": v(-31.48, 18.17) * mm});
            skPoint(sketch, "E63.25.5.0", {"position": v(-34.8, 15.5) * mm});
            skArc(sketch, "E63.26.5.0", {"start": v(-36.46, 17.95) * mm, "mid": v(-36.49, 17.83) * mm, "end": v(-36.46, 17.72) * mm});
            skArc(sketch, "E63.30.5.0", {"start": v(-34.92, 15.6) * mm, "mid": v(-34.8, 15.51) * mm, "end": v(-34.67, 15.44) * mm});
            skLineSegment(sketch, "E63.34.5.0", {"start": v(-35.95, 18.94) * mm, "end": v(-36.2, 18.45) * mm});
            skArc(sketch, "E63.37.5.0", {"start": v(-32.87, 18.97) * mm, "mid": v(-33, 19.04) * mm, "end": v(-33.15, 19.07) * mm});
            skArc(sketch, "E63.41.5.0", {"start": v(-35.76, 19.08) * mm, "mid": v(-35.87, 19.04) * mm, "end": v(-35.95, 18.94) * mm});
            skLineSegment(sketch, "E63.45.5.0", {"start": v(-36.46, 17.95) * mm, "end": v(-36.2, 18.45) * mm});
            skArc(sketch, "E63.3.6.0", {"start": v(-34.57, 11.23) * mm, "mid": v(-33.97, 11.28) * mm, "end": v(-33.57, 11.72) * mm});
            skArc(sketch, "E63.4.6.0", {"start": v(-34.94, 6.63) * mm, "mid": v(-35.05, 7.22) * mm, "end": v(-35.55, 7.56) * mm});
            skPoint(sketch, "E63.8.6.0", {"position": v(-36.24, 11.77) * mm});
            skArc(sketch, "E63.9.6.0", {"start": v(-36.4, 11.76) * mm, "mid": v(-37.69, 11.58) * mm, "end": v(-38.95, 11.23) * mm});
            skPoint(sketch, "E63.13.6.0", {"position": v(-39.07, 11.18) * mm});
            skPoint(sketch, "E63.14.6.0", {"position": v(-39.43, 9.85) * mm});
            skArc(sketch, "E63.15.6.0", {"start": v(-37.4, 8) * mm, "mid": v(-38.43, 8.81) * mm, "end": v(-39.34, 9.75) * mm});
            skLineSegment(sketch, "E63.19.6.0", {"start": v(-37.12, 7.9) * mm, "end": v(-35.55, 7.56) * mm});
            skLineSegment(sketch, "E63.22.6.0", {"start": v(-36.1, 11.73) * mm, "end": v(-34.57, 11.23) * mm});
            skPoint(sketch, "E63.25.6.0", {"position": v(-37.27, 7.92) * mm});
            skArc(sketch, "E63.26.6.0", {"start": v(-39.4, 9.98) * mm, "mid": v(-39.4, 9.86) * mm, "end": v(-39.34, 9.75) * mm});
            skArc(sketch, "E63.30.6.0", {"start": v(-37.4, 8) * mm, "mid": v(-37.27, 7.94) * mm, "end": v(-37.12, 7.9) * mm});
            skLineSegment(sketch, "E63.34.6.0", {"start": v(-39.1, 11.05) * mm, "end": v(-39.25, 10.52) * mm});
            skArc(sketch, "E63.37.6.0", {"start": v(-36.1, 11.73) * mm, "mid": v(-36.24, 11.76) * mm, "end": v(-36.4, 11.76) * mm});
            skArc(sketch, "E63.41.6.0", {"start": v(-38.95, 11.23) * mm, "mid": v(-39.05, 11.16) * mm, "end": v(-39.1, 11.05) * mm});
            skLineSegment(sketch, "E63.45.6.0", {"start": v(-39.4, 9.98) * mm, "end": v(-39.25, 10.52) * mm});
            skArc(sketch, "E63.3.7.0", {"start": v(-36.15, 3.8) * mm, "mid": v(-35.57, 3.97) * mm, "end": v(-35.28, 4.49) * mm});
            skArc(sketch, "E63.4.7.0", {"start": v(-35.55, -0.78) * mm, "mid": v(-35.79, -0.23) * mm, "end": v(-36.35, 0) * mm});
            skPoint(sketch, "E63.8.7.0", {"position": v(-37.9, 3.98) * mm});
            skArc(sketch, "E63.9.7.0", {"start": v(-38.04, 3.94) * mm, "mid": v(-39.27, 3.5) * mm, "end": v(-40.43, 2.89) * mm});
            skPoint(sketch, "E63.13.7.0", {"position": v(-40.54, 2.81) * mm});
            skPoint(sketch, "E63.14.7.0", {"position": v(-40.61, 1.44) * mm});
            skArc(sketch, "E63.15.7.0", {"start": v(-38.25, 0.06) * mm, "mid": v(-39.42, 0.63) * mm, "end": v(-40.5, 1.36) * mm});
            skLineSegment(sketch, "E63.19.7.0", {"start": v(-37.95, 0) * mm, "end": v(-36.35, 0) * mm});
            skLineSegment(sketch, "E63.22.7.0", {"start": v(-37.74, 3.97) * mm, "end": v(-36.15, 3.8) * mm});
            skPoint(sketch, "E63.25.7.0", {"position": v(-38.1, 0) * mm});
            skArc(sketch, "E63.26.7.0", {"start": v(-40.6, 1.57) * mm, "mid": v(-40.58, 1.45) * mm, "end": v(-40.5, 1.36) * mm});
            skArc(sketch, "E63.30.7.0", {"start": v(-38.25, 0.06) * mm, "mid": v(-38.1, 0.01) * mm, "end": v(-37.95, 0) * mm});
            skLineSegment(sketch, "E63.34.7.0", {"start": v(-40.55, 2.68) * mm, "end": v(-40.58, 2.13) * mm});
            skArc(sketch, "E63.37.7.0", {"start": v(-37.74, 3.97) * mm, "mid": v(-37.9, 3.97) * mm, "end": v(-38.04, 3.94) * mm});
            skArc(sketch, "E63.41.7.0", {"start": v(-40.43, 2.89) * mm, "mid": v(-40.51, 2.8) * mm, "end": v(-40.55, 2.68) * mm});
            skLineSegment(sketch, "E63.45.7.0", {"start": v(-40.6, 1.57) * mm, "end": v(-40.58, 2.13) * mm});
            skArc(sketch, "E63.3.8.0", {"start": v(-36.15, -3.8) * mm, "mid": v(-35.62, -3.52) * mm, "end": v(-35.44, -2.94) * mm});
            skArc(sketch, "E63.4.8.0", {"start": v(-34.61, -8.15) * mm, "mid": v(-34.96, -7.66) * mm, "end": v(-35.55, -7.56) * mm});
            skPoint(sketch, "E63.8.8.0", {"position": v(-37.9, -3.98) * mm});
            skArc(sketch, "E63.9.8.0", {"start": v(-38.03, -4.06) * mm, "mid": v(-39.14, -4.75) * mm, "end": v(-40.15, -5.58) * mm});
            skPoint(sketch, "E63.13.8.0", {"position": v(-40.24, -5.68) * mm});
            skPoint(sketch, "E63.14.8.0", {"position": v(-40.03, -7.04) * mm});
            skArc(sketch, "E63.15.8.0", {"start": v(-37.42, -7.9) * mm, "mid": v(-38.7, -7.58) * mm, "end": v(-39.9, -7.1) * mm});
            skLineSegment(sketch, "E63.19.8.0", {"start": v(-37.12, -7.9) * mm, "end": v(-35.55, -7.56) * mm});
            skLineSegment(sketch, "E63.22.8.0", {"start": v(-37.74, -3.97) * mm, "end": v(-36.15, -3.8) * mm});
            skPoint(sketch, "E63.25.8.0", {"position": v(-37.27, -7.92) * mm});
            skArc(sketch, "E63.26.8.0", {"start": v(-40.05, -6.9) * mm, "mid": v(-40, -7.02) * mm, "end": v(-39.9, -7.1) * mm});
            skArc(sketch, "E63.30.8.0", {"start": v(-37.42, -7.9) * mm, "mid": v(-37.27, -7.9) * mm, "end": v(-37.12, -7.9) * mm});
            skLineSegment(sketch, "E63.34.8.0", {"start": v(-40.22, -5.8) * mm, "end": v(-40.13, -6.36) * mm});
            skArc(sketch, "E63.37.8.0", {"start": v(-37.74, -3.97) * mm, "mid": v(-37.9, -4) * mm, "end": v(-38.03, -4.06) * mm});
            skArc(sketch, "E63.41.8.0", {"start": v(-40.15, -5.58) * mm, "mid": v(-40.21, -5.69) * mm, "end": v(-40.22, -5.8) * mm});
            skLineSegment(sketch, "E63.45.8.0", {"start": v(-40.05, -6.9) * mm, "end": v(-40.13, -6.36) * mm});
            skArc(sketch, "E63.3.9.0", {"start": v(-34.57, -11.23) * mm, "mid": v(-34.1, -10.84) * mm, "end": v(-34.05, -10.25) * mm});
            skArc(sketch, "E63.4.9.0", {"start": v(-32.16, -15.17) * mm, "mid": v(-32.6, -14.76) * mm, "end": v(-33.2, -14.78) * mm});
            skPoint(sketch, "E63.8.9.0", {"position": v(-36.24, -11.77) * mm});
            skArc(sketch, "E63.9.9.0", {"start": v(-36.36, -11.87) * mm, "mid": v(-37.3, -12.78) * mm, "end": v(-38.1, -13.8) * mm});
            skPoint(sketch, "E63.13.9.0", {"position": v(-38.18, -13.92) * mm});
            skPoint(sketch, "E63.14.9.0", {"position": v(-37.69, -15.2) * mm});
            skArc(sketch, "E63.15.9.0", {"start": v(-34.96, -15.5) * mm, "mid": v(-36.27, -15.46) * mm, "end": v(-37.56, -15.24) * mm});
            skLineSegment(sketch, "E63.19.9.0", {"start": v(-34.67, -15.44) * mm, "end": v(-33.2, -14.78) * mm});
            skLineSegment(sketch, "E63.22.9.0", {"start": v(-36.1, -11.73) * mm, "end": v(-34.57, -11.23) * mm});
            skPoint(sketch, "E63.25.9.0", {"position": v(-34.8, -15.5) * mm});
            skArc(sketch, "E63.26.9.0", {"start": v(-37.74, -15.08) * mm, "mid": v(-37.67, -15.18) * mm, "end": v(-37.56, -15.24) * mm});
            skArc(sketch, "E63.30.9.0", {"start": v(-34.96, -15.5) * mm, "mid": v(-34.81, -15.48) * mm, "end": v(-34.67, -15.44) * mm});
            skLineSegment(sketch, "E63.34.9.0", {"start": v(-38.13, -14.04) * mm, "end": v(-37.94, -14.56) * mm});
            skArc(sketch, "E63.37.9.0", {"start": v(-36.1, -11.73) * mm, "mid": v(-36.23, -11.79) * mm, "end": v(-36.36, -11.87) * mm});
            skArc(sketch, "E63.41.9.0", {"start": v(-38.1, -13.8) * mm, "mid": v(-38.15, -13.92) * mm, "end": v(-38.13, -14.04) * mm});
            skLineSegment(sketch, "E63.45.9.0", {"start": v(-37.74, -15.08) * mm, "end": v(-37.94, -14.56) * mm});
            skArc(sketch, "E63.3.10.0", {"start": v(-31.48, -18.17) * mm, "mid": v(-31.1, -17.7) * mm, "end": v(-31.18, -17.1) * mm});
            skArc(sketch, "E63.4.10.0", {"start": v(-28.3, -21.52) * mm, "mid": v(-28.82, -21.22) * mm, "end": v(-29.4, -21.36) * mm});
            skPoint(sketch, "E63.8.10.0", {"position": v(-33, -19.05) * mm});
            skArc(sketch, "E63.9.10.0", {"start": v(-33.1, -19.17) * mm, "mid": v(-33.83, -20.26) * mm, "end": v(-34.4, -21.43) * mm});
            skPoint(sketch, "E63.13.10.0", {"position": v(-34.45, -21.55) * mm});
            skPoint(sketch, "E63.14.10.0", {"position": v(-33.7, -22.7) * mm});
            skArc(sketch, "E63.15.10.0", {"start": v(-30.98, -22.43) * mm, "mid": v(-32.26, -22.66) * mm, "end": v(-33.57, -22.71) * mm});
            skLineSegment(sketch, "E63.19.10.0", {"start": v(-30.7, -22.3) * mm, "end": v(-29.4, -21.36) * mm});
            skLineSegment(sketch, "E63.22.10.0", {"start": v(-32.87, -18.97) * mm, "end": v(-31.48, -18.17) * mm});
            skPoint(sketch, "E63.25.10.0", {"position": v(-30.82, -22.4) * mm});
            skArc(sketch, "E63.26.10.0", {"start": v(-33.78, -22.6) * mm, "mid": v(-33.69, -22.68) * mm, "end": v(-33.57, -22.71) * mm});
            skArc(sketch, "E63.30.10.0", {"start": v(-30.98, -22.43) * mm, "mid": v(-30.83, -22.38) * mm, "end": v(-30.7, -22.3) * mm});
            skLineSegment(sketch, "E63.34.10.0", {"start": v(-34.38, -21.66) * mm, "end": v(-34.08, -22.13) * mm});
            skArc(sketch, "E63.37.10.0", {"start": v(-32.87, -18.97) * mm, "mid": v(-32.99, -19.06) * mm, "end": v(-33.1, -19.17) * mm});
            skArc(sketch, "E63.41.10.0", {"start": v(-34.4, -21.43) * mm, "mid": v(-34.42, -21.55) * mm, "end": v(-34.38, -21.66) * mm});
            skLineSegment(sketch, "E63.45.10.0", {"start": v(-33.78, -22.6) * mm, "end": v(-34.08, -22.13) * mm});
            skArc(sketch, "E63.3.11.0", {"start": v(-27, -24.32) * mm, "mid": v(-26.75, -23.78) * mm, "end": v(-26.94, -23.21) * mm});
            skArc(sketch, "E63.4.11.0", {"start": v(-23.21, -26.94) * mm, "mid": v(-23.78, -26.75) * mm, "end": v(-24.32, -27) * mm});
            skPoint(sketch, "E63.8.11.0", {"position": v(-28.31, -25.5) * mm});
            skArc(sketch, "E63.9.11.0", {"start": v(-28.38, -25.63) * mm, "mid": v(-28.88, -26.85) * mm, "end": v(-29.2, -28.11) * mm});
            skPoint(sketch, "E63.13.11.0", {"position": v(-29.22, -28.25) * mm});
            skPoint(sketch, "E63.14.11.0", {"position": v(-28.25, -29.22) * mm});
            skArc(sketch, "E63.15.11.0", {"start": v(-25.63, -28.38) * mm, "mid": v(-26.85, -28.88) * mm, "end": v(-28.11, -29.2) * mm});
            skLineSegment(sketch, "E63.19.11.0", {"start": v(-25.4, -28.2) * mm, "end": v(-24.32, -27) * mm});
            skLineSegment(sketch, "E63.22.11.0", {"start": v(-28.2, -25.4) * mm, "end": v(-27, -24.32) * mm});
            skPoint(sketch, "E63.25.11.0", {"position": v(-25.5, -28.31) * mm});
            skArc(sketch, "E63.26.11.0", {"start": v(-28.34, -29.13) * mm, "mid": v(-28.24, -29.19) * mm, "end": v(-28.11, -29.2) * mm});
            skArc(sketch, "E63.30.11.0", {"start": v(-25.63, -28.38) * mm, "mid": v(-25.5, -28.3) * mm, "end": v(-25.4, -28.2) * mm});
            skLineSegment(sketch, "E63.34.11.0", {"start": v(-29.13, -28.34) * mm, "end": v(-28.73, -28.73) * mm});
            skArc(sketch, "E63.37.11.0", {"start": v(-28.2, -25.4) * mm, "mid": v(-28.3, -25.5) * mm, "end": v(-28.38, -25.63) * mm});
            skArc(sketch, "E63.41.11.0", {"start": v(-29.2, -28.11) * mm, "mid": v(-29.19, -28.24) * mm, "end": v(-29.13, -28.34) * mm});
            skLineSegment(sketch, "E63.45.11.0", {"start": v(-28.34, -29.13) * mm, "end": v(-28.73, -28.73) * mm});
            skArc(sketch, "E63.3.12.0", {"start": v(-21.36, -29.4) * mm, "mid": v(-21.22, -28.82) * mm, "end": v(-21.52, -28.3) * mm});
            skArc(sketch, "E63.4.12.0", {"start": v(-17.1, -31.18) * mm, "mid": v(-17.7, -31.1) * mm, "end": v(-18.17, -31.48) * mm});
            skPoint(sketch, "E63.8.12.0", {"position": v(-22.4, -30.82) * mm});
            skArc(sketch, "E63.9.12.0", {"start": v(-22.43, -30.98) * mm, "mid": v(-22.66, -32.26) * mm, "end": v(-22.71, -33.57) * mm});
            skPoint(sketch, "E63.13.12.0", {"position": v(-22.7, -33.7) * mm});
            skPoint(sketch, "E63.14.12.0", {"position": v(-21.55, -34.45) * mm});
            skArc(sketch, "E63.15.12.0", {"start": v(-19.17, -33.1) * mm, "mid": v(-20.26, -33.83) * mm, "end": v(-21.43, -34.4) * mm});
            skLineSegment(sketch, "E63.19.12.0", {"start": v(-18.97, -32.87) * mm, "end": v(-18.17, -31.48) * mm});
            skLineSegment(sketch, "E63.22.12.0", {"start": v(-22.3, -30.7) * mm, "end": v(-21.36, -29.4) * mm});
            skPoint(sketch, "E63.25.12.0", {"position": v(-19.05, -33) * mm});
            skArc(sketch, "E63.26.12.0", {"start": v(-21.66, -34.38) * mm, "mid": v(-21.55, -34.42) * mm, "end": v(-21.43, -34.4) * mm});
            skArc(sketch, "E63.30.12.0", {"start": v(-19.17, -33.1) * mm, "mid": v(-19.06, -32.99) * mm, "end": v(-18.97, -32.87) * mm});
            skLineSegment(sketch, "E63.34.12.0", {"start": v(-22.6, -33.78) * mm, "end": v(-22.13, -34.08) * mm});
            skArc(sketch, "E63.37.12.0", {"start": v(-22.3, -30.7) * mm, "mid": v(-22.38, -30.83) * mm, "end": v(-22.43, -30.98) * mm});
            skArc(sketch, "E63.41.12.0", {"start": v(-22.71, -33.57) * mm, "mid": v(-22.68, -33.69) * mm, "end": v(-22.6, -33.78) * mm});
            skLineSegment(sketch, "E63.45.12.0", {"start": v(-21.66, -34.38) * mm, "end": v(-22.13, -34.08) * mm});
            skArc(sketch, "E63.3.13.0", {"start": v(-14.78, -33.2) * mm, "mid": v(-14.76, -32.6) * mm, "end": v(-15.17, -32.16) * mm});
            skArc(sketch, "E63.4.13.0", {"start": v(-10.25, -34.05) * mm, "mid": v(-10.84, -34.1) * mm, "end": v(-11.23, -34.57) * mm});
            skPoint(sketch, "E63.8.13.0", {"position": v(-15.5, -34.8) * mm});
            skArc(sketch, "E63.9.13.0", {"start": v(-15.5, -34.96) * mm, "mid": v(-15.46, -36.27) * mm, "end": v(-15.24, -37.56) * mm});
            skPoint(sketch, "E63.13.13.0", {"position": v(-15.2, -37.69) * mm});
            skPoint(sketch, "E63.14.13.0", {"position": v(-13.92, -38.18) * mm});
            skArc(sketch, "E63.15.13.0", {"start": v(-11.87, -36.36) * mm, "mid": v(-12.78, -37.3) * mm, "end": v(-13.8, -38.1) * mm});
            skLineSegment(sketch, "E63.19.13.0", {"start": v(-11.73, -36.1) * mm, "end": v(-11.23, -34.57) * mm});
            skLineSegment(sketch, "E63.22.13.0", {"start": v(-15.44, -34.67) * mm, "end": v(-14.78, -33.2) * mm});
            skPoint(sketch, "E63.25.13.0", {"position": v(-11.77, -36.24) * mm});
            skArc(sketch, "E63.26.13.0", {"start": v(-14.04, -38.13) * mm, "mid": v(-13.92, -38.15) * mm, "end": v(-13.8, -38.1) * mm});
            skArc(sketch, "E63.30.13.0", {"start": v(-11.87, -36.36) * mm, "mid": v(-11.79, -36.23) * mm, "end": v(-11.73, -36.1) * mm});
            skLineSegment(sketch, "E63.34.13.0", {"start": v(-15.08, -37.74) * mm, "end": v(-14.56, -37.94) * mm});
            skArc(sketch, "E63.37.13.0", {"start": v(-15.44, -34.67) * mm, "mid": v(-15.48, -34.81) * mm, "end": v(-15.5, -34.96) * mm});
            skArc(sketch, "E63.41.13.0", {"start": v(-15.24, -37.56) * mm, "mid": v(-15.18, -37.67) * mm, "end": v(-15.08, -37.74) * mm});
            skLineSegment(sketch, "E63.45.13.0", {"start": v(-14.04, -38.13) * mm, "end": v(-14.56, -37.94) * mm});
            skArc(sketch, "E63.3.14.0", {"start": v(-7.56, -35.55) * mm, "mid": v(-7.66, -34.96) * mm, "end": v(-8.15, -34.61) * mm});
            skArc(sketch, "E63.4.14.0", {"start": v(-2.94, -35.44) * mm, "mid": v(-3.52, -35.62) * mm, "end": v(-3.8, -36.15) * mm});
            skPoint(sketch, "E63.8.14.0", {"position": v(-7.92, -37.27) * mm});
            skArc(sketch, "E63.9.14.0", {"start": v(-7.9, -37.42) * mm, "mid": v(-7.58, -38.7) * mm, "end": v(-7.1, -39.9) * mm});
            skPoint(sketch, "E63.13.14.0", {"position": v(-7.04, -40.03) * mm});
            skPoint(sketch, "E63.14.14.0", {"position": v(-5.68, -40.24) * mm});
            skArc(sketch, "E63.15.14.0", {"start": v(-4.06, -38.03) * mm, "mid": v(-4.75, -39.14) * mm, "end": v(-5.58, -40.15) * mm});
            skLineSegment(sketch, "E63.19.14.0", {"start": v(-3.97, -37.74) * mm, "end": v(-3.8, -36.15) * mm});
            skLineSegment(sketch, "E63.22.14.0", {"start": v(-7.9, -37.12) * mm, "end": v(-7.56, -35.55) * mm});
            skPoint(sketch, "E63.25.14.0", {"position": v(-3.98, -37.9) * mm});
            skArc(sketch, "E63.26.14.0", {"start": v(-5.8, -40.22) * mm, "mid": v(-5.69, -40.21) * mm, "end": v(-5.58, -40.15) * mm});
            skArc(sketch, "E63.30.14.0", {"start": v(-4.06, -38.03) * mm, "mid": v(-4, -37.9) * mm, "end": v(-3.97, -37.74) * mm});
            skLineSegment(sketch, "E63.34.14.0", {"start": v(-6.9, -40.05) * mm, "end": v(-6.36, -40.13) * mm});
            skArc(sketch, "E63.37.14.0", {"start": v(-7.9, -37.12) * mm, "mid": v(-7.9, -37.27) * mm, "end": v(-7.9, -37.42) * mm});
            skArc(sketch, "E63.41.14.0", {"start": v(-7.1, -39.9) * mm, "mid": v(-7.02, -40) * mm, "end": v(-6.9, -40.05) * mm});
            skLineSegment(sketch, "E63.45.14.0", {"start": v(-5.8, -40.22) * mm, "end": v(-6.36, -40.13) * mm});
            skArc(sketch, "E63.3.15.0", {"start": v(0, -36.35) * mm, "mid": v(-0.23, -35.79) * mm, "end": v(-0.78, -35.55) * mm});
            skArc(sketch, "E63.4.15.0", {"start": v(4.49, -35.28) * mm, "mid": v(3.97, -35.57) * mm, "end": v(3.8, -36.15) * mm});
            skPoint(sketch, "E63.8.15.0", {"position": v(0, -38.1) * mm});
            skArc(sketch, "E63.9.15.0", {"start": v(0.06, -38.25) * mm, "mid": v(0.63, -39.42) * mm, "end": v(1.36, -40.5) * mm});
            skPoint(sketch, "E63.13.15.0", {"position": v(1.44, -40.61) * mm});
            skPoint(sketch, "E63.14.15.0", {"position": v(2.81, -40.54) * mm});
            skArc(sketch, "E63.15.15.0", {"start": v(3.94, -38.04) * mm, "mid": v(3.5, -39.27) * mm, "end": v(2.89, -40.43) * mm});
            skLineSegment(sketch, "E63.19.15.0", {"start": v(3.97, -37.74) * mm, "end": v(3.8, -36.15) * mm});
            skLineSegment(sketch, "E63.22.15.0", {"start": v(0, -37.95) * mm, "end": v(0, -36.35) * mm});
            skPoint(sketch, "E63.25.15.0", {"position": v(3.98, -37.9) * mm});
            skArc(sketch, "E63.26.15.0", {"start": v(2.68, -40.55) * mm, "mid": v(2.8, -40.51) * mm, "end": v(2.89, -40.43) * mm});
            skArc(sketch, "E63.30.15.0", {"start": v(3.94, -38.04) * mm, "mid": v(3.97, -37.9) * mm, "end": v(3.97, -37.74) * mm});
            skLineSegment(sketch, "E63.34.15.0", {"start": v(1.57, -40.6) * mm, "end": v(2.13, -40.58) * mm});
            skArc(sketch, "E63.37.15.0", {"start": v(0, -37.95) * mm, "mid": v(0.01, -38.1) * mm, "end": v(0.06, -38.25) * mm});
            skArc(sketch, "E63.41.15.0", {"start": v(1.36, -40.5) * mm, "mid": v(1.45, -40.58) * mm, "end": v(1.57, -40.6) * mm});
            skLineSegment(sketch, "E63.45.15.0", {"start": v(2.68, -40.55) * mm, "end": v(2.13, -40.58) * mm});
            skArc(sketch, "E63.3.16.0", {"start": v(7.56, -35.55) * mm, "mid": v(7.22, -35.05) * mm, "end": v(6.63, -34.94) * mm});
            skArc(sketch, "E63.4.16.0", {"start": v(11.72, -33.57) * mm, "mid": v(11.28, -33.97) * mm, "end": v(11.23, -34.57) * mm});
            skPoint(sketch, "E63.8.16.0", {"position": v(7.92, -37.27) * mm});
            skArc(sketch, "E63.9.16.0", {"start": v(8, -37.4) * mm, "mid": v(8.81, -38.43) * mm, "end": v(9.75, -39.34) * mm});
            skPoint(sketch, "E63.13.16.0", {"position": v(9.85, -39.43) * mm});
            skPoint(sketch, "E63.14.16.0", {"position": v(11.18, -39.07) * mm});
            skArc(sketch, "E63.15.16.0", {"start": v(11.76, -36.4) * mm, "mid": v(11.58, -37.69) * mm, "end": v(11.23, -38.95) * mm});
            skLineSegment(sketch, "E63.19.16.0", {"start": v(11.73, -36.1) * mm, "end": v(11.23, -34.57) * mm});
            skLineSegment(sketch, "E63.22.16.0", {"start": v(7.9, -37.12) * mm, "end": v(7.56, -35.55) * mm});
            skPoint(sketch, "E63.25.16.0", {"position": v(11.77, -36.24) * mm});
            skArc(sketch, "E63.26.16.0", {"start": v(11.05, -39.1) * mm, "mid": v(11.16, -39.05) * mm, "end": v(11.23, -38.95) * mm});
            skArc(sketch, "E63.30.16.0", {"start": v(11.76, -36.4) * mm, "mid": v(11.76, -36.24) * mm, "end": v(11.73, -36.1) * mm});
            skLineSegment(sketch, "E63.34.16.0", {"start": v(9.98, -39.4) * mm, "end": v(10.52, -39.25) * mm});
            skArc(sketch, "E63.37.16.0", {"start": v(7.9, -37.12) * mm, "mid": v(7.94, -37.27) * mm, "end": v(8, -37.4) * mm});
            skArc(sketch, "E63.41.16.0", {"start": v(9.75, -39.34) * mm, "mid": v(9.86, -39.4) * mm, "end": v(9.98, -39.4) * mm});
            skLineSegment(sketch, "E63.45.16.0", {"start": v(11.05, -39.1) * mm, "end": v(10.52, -39.25) * mm});
            skArc(sketch, "E63.3.17.0", {"start": v(14.78, -33.2) * mm, "mid": v(14.35, -32.79) * mm, "end": v(13.75, -32.8) * mm});
            skArc(sketch, "E63.4.17.0", {"start": v(18.45, -30.4) * mm, "mid": v(18.1, -30.88) * mm, "end": v(18.17, -31.48) * mm});
            skPoint(sketch, "E63.8.17.0", {"position": v(15.5, -34.8) * mm});
            skArc(sketch, "E63.9.17.0", {"start": v(15.6, -34.92) * mm, "mid": v(16.6, -35.76) * mm, "end": v(17.72, -36.46) * mm});
            skPoint(sketch, "E63.13.17.0", {"position": v(17.83, -36.52) * mm});
            skPoint(sketch, "E63.14.17.0", {"position": v(19.06, -35.9) * mm});
            skArc(sketch, "E63.15.17.0", {"start": v(19.07, -33.15) * mm, "mid": v(19.17, -34.46) * mm, "end": v(19.08, -35.76) * mm});
            skLineSegment(sketch, "E63.19.17.0", {"start": v(18.97, -32.87) * mm, "end": v(18.17, -31.48) * mm});
            skLineSegment(sketch, "E63.22.17.0", {"start": v(15.44, -34.67) * mm, "end": v(14.78, -33.2) * mm});
            skPoint(sketch, "E63.25.17.0", {"position": v(19.05, -33) * mm});
            skArc(sketch, "E63.26.17.0", {"start": v(18.94, -35.95) * mm, "mid": v(19.04, -35.87) * mm, "end": v(19.08, -35.76) * mm});
            skArc(sketch, "E63.30.17.0", {"start": v(19.07, -33.15) * mm, "mid": v(19.04, -33) * mm, "end": v(18.97, -32.87) * mm});
            skLineSegment(sketch, "E63.34.17.0", {"start": v(17.95, -36.46) * mm, "end": v(18.45, -36.2) * mm});
            skArc(sketch, "E63.37.17.0", {"start": v(15.44, -34.67) * mm, "mid": v(15.51, -34.8) * mm, "end": v(15.6, -34.92) * mm});
            skArc(sketch, "E63.41.17.0", {"start": v(17.72, -36.46) * mm, "mid": v(17.83, -36.49) * mm, "end": v(17.95, -36.46) * mm});
            skLineSegment(sketch, "E63.45.17.0", {"start": v(18.94, -35.95) * mm, "end": v(18.45, -36.2) * mm});
            skArc(sketch, "E63.3.18.0", {"start": v(21.36, -29.4) * mm, "mid": v(20.85, -29.09) * mm, "end": v(20.27, -29.22) * mm});
            skArc(sketch, "E63.4.18.0", {"start": v(24.37, -25.9) * mm, "mid": v(24.12, -26.45) * mm, "end": v(24.32, -27) * mm});
            skPoint(sketch, "E63.8.18.0", {"position": v(22.4, -30.82) * mm});
            skArc(sketch, "E63.9.18.0", {"start": v(22.53, -30.9) * mm, "mid": v(23.68, -31.52) * mm, "end": v(24.9, -31.98) * mm});
            skPoint(sketch, "E63.13.18.0", {"position": v(25.04, -32.01) * mm});
            skPoint(sketch, "E63.14.18.0", {"position": v(26.1, -31.15) * mm});
            skArc(sketch, "E63.15.18.0", {"start": v(25.55, -28.46) * mm, "mid": v(25.91, -29.72) * mm, "end": v(26.1, -31.01) * mm});
            skLineSegment(sketch, "E63.19.18.0", {"start": v(25.4, -28.2) * mm, "end": v(24.32, -27) * mm});
            skLineSegment(sketch, "E63.22.18.0", {"start": v(22.3, -30.7) * mm, "end": v(21.36, -29.4) * mm});
            skPoint(sketch, "E63.25.18.0", {"position": v(25.5, -28.31) * mm});
            skArc(sketch, "E63.26.18.0", {"start": v(26, -31.23) * mm, "mid": v(26.08, -31.13) * mm, "end": v(26.1, -31.01) * mm});
            skArc(sketch, "E63.30.18.0", {"start": v(25.55, -28.46) * mm, "mid": v(25.48, -28.32) * mm, "end": v(25.4, -28.2) * mm});
            skLineSegment(sketch, "E63.34.18.0", {"start": v(25.14, -31.93) * mm, "end": v(25.57, -31.58) * mm});
            skArc(sketch, "E63.37.18.0", {"start": v(22.3, -30.7) * mm, "mid": v(22.4, -30.82) * mm, "end": v(22.53, -30.9) * mm});
            skArc(sketch, "E63.41.18.0", {"start": v(24.9, -31.98) * mm, "mid": v(25.03, -31.98) * mm, "end": v(25.14, -31.93) * mm});
            skLineSegment(sketch, "E63.45.18.0", {"start": v(26, -31.23) * mm, "end": v(25.57, -31.58) * mm});
            skArc(sketch, "E63.3.19.0", {"start": v(27, -24.32) * mm, "mid": v(26.45, -24.12) * mm, "end": v(25.9, -24.37) * mm});
            skArc(sketch, "E63.4.19.0", {"start": v(29.22, -20.27) * mm, "mid": v(29.09, -20.85) * mm, "end": v(29.4, -21.36) * mm});
            skPoint(sketch, "E63.8.19.0", {"position": v(28.31, -25.5) * mm});
            skArc(sketch, "E63.9.19.0", {"start": v(28.46, -25.55) * mm, "mid": v(29.72, -25.91) * mm, "end": v(31.01, -26.1) * mm});
            skPoint(sketch, "E63.13.19.0", {"position": v(31.15, -26.1) * mm});
            skPoint(sketch, "E63.14.19.0", {"position": v(32.01, -25.04) * mm});
            skArc(sketch, "E63.15.19.0", {"start": v(30.9, -22.53) * mm, "mid": v(31.52, -23.68) * mm, "end": v(31.98, -24.9) * mm});
            skLineSegment(sketch, "E63.19.19.0", {"start": v(30.7, -22.3) * mm, "end": v(29.4, -21.36) * mm});
            skLineSegment(sketch, "E63.22.19.0", {"start": v(28.2, -25.4) * mm, "end": v(27, -24.32) * mm});
            skPoint(sketch, "E63.25.19.0", {"position": v(30.82, -22.4) * mm});
            skArc(sketch, "E63.26.19.0", {"start": v(31.93, -25.14) * mm, "mid": v(31.98, -25.03) * mm, "end": v(31.98, -24.9) * mm});
            skArc(sketch, "E63.30.19.0", {"start": v(30.9, -22.53) * mm, "mid": v(30.82, -22.4) * mm, "end": v(30.7, -22.3) * mm});
            skLineSegment(sketch, "E63.34.19.0", {"start": v(31.23, -26) * mm, "end": v(31.58, -25.57) * mm});
            skArc(sketch, "E63.37.19.0", {"start": v(28.2, -25.4) * mm, "mid": v(28.32, -25.48) * mm, "end": v(28.46, -25.55) * mm});
            skArc(sketch, "E63.41.19.0", {"start": v(31.01, -26.1) * mm, "mid": v(31.13, -26.08) * mm, "end": v(31.23, -26) * mm});
            skLineSegment(sketch, "E63.45.19.0", {"start": v(31.93, -25.14) * mm, "end": v(31.58, -25.57) * mm});
            skArc(sketch, "E63.3.20.0", {"start": v(31.48, -18.17) * mm, "mid": v(30.88, -18.1) * mm, "end": v(30.4, -18.45) * mm});
            skArc(sketch, "E63.4.20.0", {"start": v(32.8, -13.75) * mm, "mid": v(32.79, -14.35) * mm, "end": v(33.2, -14.78) * mm});
            skPoint(sketch, "E63.8.20.0", {"position": v(33, -19.05) * mm});
            skArc(sketch, "E63.9.20.0", {"start": v(33.15, -19.07) * mm, "mid": v(34.46, -19.17) * mm, "end": v(35.76, -19.08) * mm});
            skPoint(sketch, "E63.13.20.0", {"position": v(35.9, -19.06) * mm});
            skPoint(sketch, "E63.14.20.0", {"position": v(36.52, -17.83) * mm});
            skArc(sketch, "E63.15.20.0", {"start": v(34.92, -15.6) * mm, "mid": v(35.76, -16.6) * mm, "end": v(36.46, -17.72) * mm});
            skLineSegment(sketch, "E63.19.20.0", {"start": v(34.67, -15.44) * mm, "end": v(33.2, -14.78) * mm});
            skLineSegment(sketch, "E63.22.20.0", {"start": v(32.87, -18.97) * mm, "end": v(31.48, -18.17) * mm});
            skPoint(sketch, "E63.25.20.0", {"position": v(34.8, -15.5) * mm});
            skArc(sketch, "E63.26.20.0", {"start": v(36.46, -17.95) * mm, "mid": v(36.49, -17.83) * mm, "end": v(36.46, -17.72) * mm});
            skArc(sketch, "E63.30.20.0", {"start": v(34.92, -15.6) * mm, "mid": v(34.8, -15.51) * mm, "end": v(34.67, -15.44) * mm});
            skLineSegment(sketch, "E63.34.20.0", {"start": v(35.95, -18.94) * mm, "end": v(36.2, -18.45) * mm});
            skArc(sketch, "E63.37.20.0", {"start": v(32.87, -18.97) * mm, "mid": v(33, -19.04) * mm, "end": v(33.15, -19.07) * mm});
            skArc(sketch, "E63.41.20.0", {"start": v(35.76, -19.08) * mm, "mid": v(35.87, -19.04) * mm, "end": v(35.95, -18.94) * mm});
            skLineSegment(sketch, "E63.45.20.0", {"start": v(36.46, -17.95) * mm, "end": v(36.2, -18.45) * mm});
            skArc(sketch, "E63.3.21.0", {"start": v(34.57, -11.23) * mm, "mid": v(33.97, -11.28) * mm, "end": v(33.57, -11.72) * mm});
            skArc(sketch, "E63.4.21.0", {"start": v(34.94, -6.63) * mm, "mid": v(35.05, -7.22) * mm, "end": v(35.55, -7.56) * mm});
            skPoint(sketch, "E63.8.21.0", {"position": v(36.24, -11.77) * mm});
            skArc(sketch, "E63.9.21.0", {"start": v(36.4, -11.76) * mm, "mid": v(37.69, -11.58) * mm, "end": v(38.95, -11.23) * mm});
            skPoint(sketch, "E63.13.21.0", {"position": v(39.07, -11.18) * mm});
            skPoint(sketch, "E63.14.21.0", {"position": v(39.43, -9.85) * mm});
            skArc(sketch, "E63.15.21.0", {"start": v(37.4, -8) * mm, "mid": v(38.43, -8.81) * mm, "end": v(39.34, -9.75) * mm});
            skLineSegment(sketch, "E63.19.21.0", {"start": v(37.12, -7.9) * mm, "end": v(35.55, -7.56) * mm});
            skLineSegment(sketch, "E63.22.21.0", {"start": v(36.1, -11.73) * mm, "end": v(34.57, -11.23) * mm});
            skPoint(sketch, "E63.25.21.0", {"position": v(37.27, -7.92) * mm});
            skArc(sketch, "E63.26.21.0", {"start": v(39.4, -9.98) * mm, "mid": v(39.4, -9.86) * mm, "end": v(39.34, -9.75) * mm});
            skArc(sketch, "E63.30.21.0", {"start": v(37.4, -8) * mm, "mid": v(37.27, -7.94) * mm, "end": v(37.12, -7.9) * mm});
            skLineSegment(sketch, "E63.34.21.0", {"start": v(39.1, -11.05) * mm, "end": v(39.25, -10.52) * mm});
            skArc(sketch, "E63.37.21.0", {"start": v(36.1, -11.73) * mm, "mid": v(36.24, -11.76) * mm, "end": v(36.4, -11.76) * mm});
            skArc(sketch, "E63.41.21.0", {"start": v(38.95, -11.23) * mm, "mid": v(39.05, -11.16) * mm, "end": v(39.1, -11.05) * mm});
            skLineSegment(sketch, "E63.45.21.0", {"start": v(39.4, -9.98) * mm, "end": v(39.25, -10.52) * mm});
            skArc(sketch, "E63.3.22.0", {"start": v(36.15, -3.8) * mm, "mid": v(35.57, -3.97) * mm, "end": v(35.28, -4.49) * mm});
            skArc(sketch, "E63.4.22.0", {"start": v(35.55, 0.78) * mm, "mid": v(35.79, 0.23) * mm, "end": v(36.35, 0) * mm});
            skPoint(sketch, "E63.8.22.0", {"position": v(37.9, -3.98) * mm});
            skArc(sketch, "E63.9.22.0", {"start": v(38.04, -3.94) * mm, "mid": v(39.27, -3.5) * mm, "end": v(40.43, -2.89) * mm});
            skPoint(sketch, "E63.13.22.0", {"position": v(40.54, -2.81) * mm});
            skPoint(sketch, "E63.14.22.0", {"position": v(40.61, -1.44) * mm});
            skArc(sketch, "E63.15.22.0", {"start": v(38.25, -0.06) * mm, "mid": v(39.42, -0.63) * mm, "end": v(40.5, -1.36) * mm});
            skLineSegment(sketch, "E63.19.22.0", {"start": v(37.95, 0) * mm, "end": v(36.35, 0) * mm});
            skLineSegment(sketch, "E63.22.22.0", {"start": v(37.74, -3.97) * mm, "end": v(36.15, -3.8) * mm});
            skPoint(sketch, "E63.25.22.0", {"position": v(38.1, 0) * mm});
            skArc(sketch, "E63.26.22.0", {"start": v(40.6, -1.57) * mm, "mid": v(40.58, -1.45) * mm, "end": v(40.5, -1.36) * mm});
            skArc(sketch, "E63.30.22.0", {"start": v(38.25, -0.06) * mm, "mid": v(38.1, -0.01) * mm, "end": v(37.95, 0) * mm});
            skLineSegment(sketch, "E63.34.22.0", {"start": v(40.55, -2.68) * mm, "end": v(40.58, -2.13) * mm});
            skArc(sketch, "E63.37.22.0", {"start": v(37.74, -3.97) * mm, "mid": v(37.9, -3.97) * mm, "end": v(38.04, -3.94) * mm});
            skArc(sketch, "E63.41.22.0", {"start": v(40.43, -2.89) * mm, "mid": v(40.51, -2.8) * mm, "end": v(40.55, -2.68) * mm});
            skLineSegment(sketch, "E63.45.22.0", {"start": v(40.6, -1.57) * mm, "end": v(40.58, -2.13) * mm});
            skArc(sketch, "E63.3.23.0", {"start": v(36.15, 3.8) * mm, "mid": v(35.62, 3.52) * mm, "end": v(35.44, 2.94) * mm});
            skArc(sketch, "E63.4.23.0", {"start": v(34.61, 8.15) * mm, "mid": v(34.96, 7.66) * mm, "end": v(35.55, 7.56) * mm});
            skPoint(sketch, "E63.8.23.0", {"position": v(37.9, 3.98) * mm});
            skArc(sketch, "E63.9.23.0", {"start": v(38.03, 4.06) * mm, "mid": v(39.14, 4.75) * mm, "end": v(40.15, 5.58) * mm});
            skPoint(sketch, "E63.13.23.0", {"position": v(40.24, 5.68) * mm});
            skPoint(sketch, "E63.14.23.0", {"position": v(40.03, 7.04) * mm});
            skArc(sketch, "E63.15.23.0", {"start": v(37.42, 7.9) * mm, "mid": v(38.7, 7.58) * mm, "end": v(39.9, 7.1) * mm});
            skLineSegment(sketch, "E63.19.23.0", {"start": v(37.12, 7.9) * mm, "end": v(35.55, 7.56) * mm});
            skLineSegment(sketch, "E63.22.23.0", {"start": v(37.74, 3.97) * mm, "end": v(36.15, 3.8) * mm});
            skPoint(sketch, "E63.25.23.0", {"position": v(37.27, 7.92) * mm});
            skArc(sketch, "E63.26.23.0", {"start": v(40.05, 6.9) * mm, "mid": v(40, 7.02) * mm, "end": v(39.9, 7.1) * mm});
            skArc(sketch, "E63.30.23.0", {"start": v(37.42, 7.9) * mm, "mid": v(37.27, 7.9) * mm, "end": v(37.12, 7.9) * mm});
            skLineSegment(sketch, "E63.34.23.0", {"start": v(40.22, 5.8) * mm, "end": v(40.13, 6.36) * mm});
            skArc(sketch, "E63.37.23.0", {"start": v(37.74, 3.97) * mm, "mid": v(37.9, 4) * mm, "end": v(38.03, 4.06) * mm});
            skArc(sketch, "E63.41.23.0", {"start": v(40.15, 5.58) * mm, "mid": v(40.21, 5.69) * mm, "end": v(40.22, 5.8) * mm});
            skLineSegment(sketch, "E63.45.23.0", {"start": v(40.05, 6.9) * mm, "end": v(40.13, 6.36) * mm});
            skArc(sketch, "E63.3.24.0", {"start": v(34.57, 11.23) * mm, "mid": v(34.1, 10.84) * mm, "end": v(34.05, 10.25) * mm});
            skArc(sketch, "E63.4.24.0", {"start": v(32.16, 15.17) * mm, "mid": v(32.6, 14.76) * mm, "end": v(33.2, 14.78) * mm});
            skPoint(sketch, "E63.8.24.0", {"position": v(36.24, 11.77) * mm});
            skArc(sketch, "E63.9.24.0", {"start": v(36.36, 11.87) * mm, "mid": v(37.3, 12.78) * mm, "end": v(38.1, 13.8) * mm});
            skPoint(sketch, "E63.13.24.0", {"position": v(38.18, 13.92) * mm});
            skPoint(sketch, "E63.14.24.0", {"position": v(37.69, 15.2) * mm});
            skArc(sketch, "E63.15.24.0", {"start": v(34.96, 15.5) * mm, "mid": v(36.27, 15.46) * mm, "end": v(37.56, 15.24) * mm});
            skLineSegment(sketch, "E63.19.24.0", {"start": v(34.67, 15.44) * mm, "end": v(33.2, 14.78) * mm});
            skLineSegment(sketch, "E63.22.24.0", {"start": v(36.1, 11.73) * mm, "end": v(34.57, 11.23) * mm});
            skPoint(sketch, "E63.25.24.0", {"position": v(34.8, 15.5) * mm});
            skArc(sketch, "E63.26.24.0", {"start": v(37.74, 15.08) * mm, "mid": v(37.67, 15.18) * mm, "end": v(37.56, 15.24) * mm});
            skArc(sketch, "E63.30.24.0", {"start": v(34.96, 15.5) * mm, "mid": v(34.81, 15.48) * mm, "end": v(34.67, 15.44) * mm});
            skLineSegment(sketch, "E63.34.24.0", {"start": v(38.13, 14.04) * mm, "end": v(37.94, 14.56) * mm});
            skArc(sketch, "E63.37.24.0", {"start": v(36.1, 11.73) * mm, "mid": v(36.23, 11.79) * mm, "end": v(36.36, 11.87) * mm});
            skArc(sketch, "E63.41.24.0", {"start": v(38.1, 13.8) * mm, "mid": v(38.15, 13.92) * mm, "end": v(38.13, 14.04) * mm});
            skLineSegment(sketch, "E63.45.24.0", {"start": v(37.74, 15.08) * mm, "end": v(37.94, 14.56) * mm});
            skArc(sketch, "E63.3.25.0", {"start": v(31.48, 18.17) * mm, "mid": v(31.1, 17.7) * mm, "end": v(31.18, 17.1) * mm});
            skArc(sketch, "E63.4.25.0", {"start": v(28.3, 21.52) * mm, "mid": v(28.82, 21.22) * mm, "end": v(29.4, 21.36) * mm});
            skPoint(sketch, "E63.8.25.0", {"position": v(33, 19.05) * mm});
            skArc(sketch, "E63.9.25.0", {"start": v(33.1, 19.17) * mm, "mid": v(33.83, 20.26) * mm, "end": v(34.4, 21.43) * mm});
            skPoint(sketch, "E63.13.25.0", {"position": v(34.45, 21.55) * mm});
            skPoint(sketch, "E63.14.25.0", {"position": v(33.7, 22.7) * mm});
            skArc(sketch, "E63.15.25.0", {"start": v(30.98, 22.43) * mm, "mid": v(32.26, 22.66) * mm, "end": v(33.57, 22.71) * mm});
            skLineSegment(sketch, "E63.19.25.0", {"start": v(30.7, 22.3) * mm, "end": v(29.4, 21.36) * mm});
            skLineSegment(sketch, "E63.22.25.0", {"start": v(32.87, 18.97) * mm, "end": v(31.48, 18.17) * mm});
            skPoint(sketch, "E63.25.25.0", {"position": v(30.82, 22.4) * mm});
            skArc(sketch, "E63.26.25.0", {"start": v(33.78, 22.6) * mm, "mid": v(33.69, 22.68) * mm, "end": v(33.57, 22.71) * mm});
            skArc(sketch, "E63.30.25.0", {"start": v(30.98, 22.43) * mm, "mid": v(30.83, 22.38) * mm, "end": v(30.7, 22.3) * mm});
            skLineSegment(sketch, "E63.34.25.0", {"start": v(34.38, 21.66) * mm, "end": v(34.08, 22.13) * mm});
            skArc(sketch, "E63.37.25.0", {"start": v(32.87, 18.97) * mm, "mid": v(32.99, 19.06) * mm, "end": v(33.1, 19.17) * mm});
            skArc(sketch, "E63.41.25.0", {"start": v(34.4, 21.43) * mm, "mid": v(34.42, 21.55) * mm, "end": v(34.38, 21.66) * mm});
            skLineSegment(sketch, "E63.45.25.0", {"start": v(33.78, 22.6) * mm, "end": v(34.08, 22.13) * mm});
            skArc(sketch, "E63.3.26.0", {"start": v(27, 24.32) * mm, "mid": v(26.75, 23.78) * mm, "end": v(26.94, 23.21) * mm});
            skArc(sketch, "E63.4.26.0", {"start": v(23.21, 26.94) * mm, "mid": v(23.78, 26.75) * mm, "end": v(24.32, 27) * mm});
            skPoint(sketch, "E63.8.26.0", {"position": v(28.31, 25.5) * mm});
            skArc(sketch, "E63.9.26.0", {"start": v(28.38, 25.63) * mm, "mid": v(28.88, 26.85) * mm, "end": v(29.2, 28.11) * mm});
            skPoint(sketch, "E63.13.26.0", {"position": v(29.22, 28.25) * mm});
            skPoint(sketch, "E63.14.26.0", {"position": v(28.25, 29.22) * mm});
            skArc(sketch, "E63.15.26.0", {"start": v(25.63, 28.38) * mm, "mid": v(26.85, 28.88) * mm, "end": v(28.11, 29.2) * mm});
            skLineSegment(sketch, "E63.19.26.0", {"start": v(25.4, 28.2) * mm, "end": v(24.32, 27) * mm});
            skLineSegment(sketch, "E63.22.26.0", {"start": v(28.2, 25.4) * mm, "end": v(27, 24.32) * mm});
            skPoint(sketch, "E63.25.26.0", {"position": v(25.5, 28.31) * mm});
            skArc(sketch, "E63.26.26.0", {"start": v(28.34, 29.13) * mm, "mid": v(28.24, 29.19) * mm, "end": v(28.11, 29.2) * mm});
            skArc(sketch, "E63.30.26.0", {"start": v(25.63, 28.38) * mm, "mid": v(25.5, 28.3) * mm, "end": v(25.4, 28.2) * mm});
            skLineSegment(sketch, "E63.34.26.0", {"start": v(29.13, 28.34) * mm, "end": v(28.73, 28.73) * mm});
            skArc(sketch, "E63.37.26.0", {"start": v(28.2, 25.4) * mm, "mid": v(28.3, 25.5) * mm, "end": v(28.38, 25.63) * mm});
            skArc(sketch, "E63.41.26.0", {"start": v(29.2, 28.11) * mm, "mid": v(29.19, 28.24) * mm, "end": v(29.13, 28.34) * mm});
            skLineSegment(sketch, "E63.45.26.0", {"start": v(28.34, 29.13) * mm, "end": v(28.73, 28.73) * mm});
            skArc(sketch, "E63.3.27.0", {"start": v(21.36, 29.4) * mm, "mid": v(21.22, 28.82) * mm, "end": v(21.52, 28.3) * mm});
            skArc(sketch, "E63.4.27.0", {"start": v(17.1, 31.18) * mm, "mid": v(17.7, 31.1) * mm, "end": v(18.17, 31.48) * mm});
            skPoint(sketch, "E63.8.27.0", {"position": v(22.4, 30.82) * mm});
            skArc(sketch, "E63.9.27.0", {"start": v(22.43, 30.98) * mm, "mid": v(22.66, 32.26) * mm, "end": v(22.71, 33.57) * mm});
            skPoint(sketch, "E63.13.27.0", {"position": v(22.7, 33.7) * mm});
            skPoint(sketch, "E63.14.27.0", {"position": v(21.55, 34.45) * mm});
            skArc(sketch, "E63.15.27.0", {"start": v(19.17, 33.1) * mm, "mid": v(20.26, 33.83) * mm, "end": v(21.43, 34.4) * mm});
            skLineSegment(sketch, "E63.19.27.0", {"start": v(18.97, 32.87) * mm, "end": v(18.17, 31.48) * mm});
            skLineSegment(sketch, "E63.22.27.0", {"start": v(22.3, 30.7) * mm, "end": v(21.36, 29.4) * mm});
            skPoint(sketch, "E63.25.27.0", {"position": v(19.05, 33) * mm});
            skArc(sketch, "E63.26.27.0", {"start": v(21.66, 34.38) * mm, "mid": v(21.55, 34.42) * mm, "end": v(21.43, 34.4) * mm});
            skArc(sketch, "E63.30.27.0", {"start": v(19.17, 33.1) * mm, "mid": v(19.06, 32.99) * mm, "end": v(18.97, 32.87) * mm});
            skLineSegment(sketch, "E63.34.27.0", {"start": v(22.6, 33.78) * mm, "end": v(22.13, 34.08) * mm});
            skArc(sketch, "E63.37.27.0", {"start": v(22.3, 30.7) * mm, "mid": v(22.38, 30.83) * mm, "end": v(22.43, 30.98) * mm});
            skArc(sketch, "E63.41.27.0", {"start": v(22.71, 33.57) * mm, "mid": v(22.68, 33.69) * mm, "end": v(22.6, 33.78) * mm});
            skLineSegment(sketch, "E63.45.27.0", {"start": v(21.66, 34.38) * mm, "end": v(22.13, 34.08) * mm});
            skArc(sketch, "E63.3.28.0", {"start": v(14.78, 33.2) * mm, "mid": v(14.76, 32.6) * mm, "end": v(15.17, 32.16) * mm});
            skArc(sketch, "E63.4.28.0", {"start": v(10.25, 34.05) * mm, "mid": v(10.84, 34.1) * mm, "end": v(11.23, 34.57) * mm});
            skPoint(sketch, "E63.8.28.0", {"position": v(15.5, 34.8) * mm});
            skArc(sketch, "E63.9.28.0", {"start": v(15.5, 34.96) * mm, "mid": v(15.46, 36.27) * mm, "end": v(15.24, 37.56) * mm});
            skPoint(sketch, "E63.13.28.0", {"position": v(15.2, 37.69) * mm});
            skPoint(sketch, "E63.14.28.0", {"position": v(13.92, 38.18) * mm});
            skArc(sketch, "E63.15.28.0", {"start": v(11.87, 36.36) * mm, "mid": v(12.78, 37.3) * mm, "end": v(13.8, 38.1) * mm});
            skLineSegment(sketch, "E63.19.28.0", {"start": v(11.73, 36.1) * mm, "end": v(11.23, 34.57) * mm});
            skLineSegment(sketch, "E63.22.28.0", {"start": v(15.44, 34.67) * mm, "end": v(14.78, 33.2) * mm});
            skPoint(sketch, "E63.25.28.0", {"position": v(11.77, 36.24) * mm});
            skArc(sketch, "E63.26.28.0", {"start": v(14.04, 38.13) * mm, "mid": v(13.92, 38.15) * mm, "end": v(13.8, 38.1) * mm});
            skArc(sketch, "E63.30.28.0", {"start": v(11.87, 36.36) * mm, "mid": v(11.79, 36.23) * mm, "end": v(11.73, 36.1) * mm});
            skLineSegment(sketch, "E63.34.28.0", {"start": v(15.08, 37.74) * mm, "end": v(14.56, 37.94) * mm});
            skArc(sketch, "E63.37.28.0", {"start": v(15.44, 34.67) * mm, "mid": v(15.48, 34.81) * mm, "end": v(15.5, 34.96) * mm});
            skArc(sketch, "E63.41.28.0", {"start": v(15.24, 37.56) * mm, "mid": v(15.18, 37.67) * mm, "end": v(15.08, 37.74) * mm});
            skLineSegment(sketch, "E63.45.28.0", {"start": v(14.04, 38.13) * mm, "end": v(14.56, 37.94) * mm});
            skArc(sketch, "E63.3.29.0", {"start": v(7.56, 35.55) * mm, "mid": v(7.66, 34.96) * mm, "end": v(8.15, 34.61) * mm});
            skArc(sketch, "E63.4.29.0", {"start": v(2.94, 35.44) * mm, "mid": v(3.52, 35.62) * mm, "end": v(3.8, 36.15) * mm});
            skPoint(sketch, "E63.8.29.0", {"position": v(7.92, 37.27) * mm});
            skArc(sketch, "E63.9.29.0", {"start": v(7.9, 37.42) * mm, "mid": v(7.58, 38.7) * mm, "end": v(7.1, 39.9) * mm});
            skPoint(sketch, "E63.13.29.0", {"position": v(7.04, 40.03) * mm});
            skPoint(sketch, "E63.14.29.0", {"position": v(5.68, 40.24) * mm});
            skArc(sketch, "E63.15.29.0", {"start": v(4.06, 38.03) * mm, "mid": v(4.75, 39.14) * mm, "end": v(5.58, 40.15) * mm});
            skLineSegment(sketch, "E63.19.29.0", {"start": v(3.97, 37.74) * mm, "end": v(3.8, 36.15) * mm});
            skLineSegment(sketch, "E63.22.29.0", {"start": v(7.9, 37.12) * mm, "end": v(7.56, 35.55) * mm});
            skPoint(sketch, "E63.25.29.0", {"position": v(3.98, 37.9) * mm});
            skArc(sketch, "E63.26.29.0", {"start": v(5.8, 40.22) * mm, "mid": v(5.69, 40.21) * mm, "end": v(5.58, 40.15) * mm});
            skArc(sketch, "E63.30.29.0", {"start": v(4.06, 38.03) * mm, "mid": v(4, 37.9) * mm, "end": v(3.97, 37.74) * mm});
            skLineSegment(sketch, "E63.34.29.0", {"start": v(6.9, 40.05) * mm, "end": v(6.36, 40.13) * mm});
            skArc(sketch, "E63.37.29.0", {"start": v(7.9, 37.12) * mm, "mid": v(7.9, 37.27) * mm, "end": v(7.9, 37.42) * mm});
            skArc(sketch, "E63.41.29.0", {"start": v(7.1, 39.9) * mm, "mid": v(7.02, 40) * mm, "end": v(6.9, 40.05) * mm});
            skLineSegment(sketch, "E63.45.29.0", {"start": v(5.8, 40.22) * mm, "end": v(6.36, 40.13) * mm});
            skArc(sketch, "E64.trimOffspring", {"start": v(2.94, 35.44) * mm, "mid": v(1.86, 35.51) * mm, "end": v(0.78, 35.55) * mm});
            skArc(sketch, "E65.trimOffspring", {"start": v(10.25, 34.05) * mm, "mid": v(9.2, 34.35) * mm, "end": v(8.15, 34.61) * mm});
            skArc(sketch, "E66.trimOffspring", {"start": v(17.1, 31.18) * mm, "mid": v(16.14, 31.68) * mm, "end": v(15.17, 32.16) * mm});
            skArc(sketch, "E67.trimOffspring", {"start": v(23.21, 26.94) * mm, "mid": v(22.38, 27.64) * mm, "end": v(21.52, 28.3) * mm});
            skArc(sketch, "E68.trimOffspring", {"start": v(28.3, 21.52) * mm, "mid": v(27.64, 22.38) * mm, "end": v(26.94, 23.21) * mm});
            skArc(sketch, "E69.trimOffspring", {"start": v(32.16, 15.17) * mm, "mid": v(31.68, 16.14) * mm, "end": v(31.18, 17.1) * mm});
            skArc(sketch, "E70.trimOffspring", {"start": v(34.61, 8.15) * mm, "mid": v(34.35, 9.2) * mm, "end": v(34.05, 10.25) * mm});
            skArc(sketch, "E71.trimOffspring", {"start": v(35.55, 0.78) * mm, "mid": v(35.51, 1.86) * mm, "end": v(35.44, 2.94) * mm});
            skArc(sketch, "E72.trimOffspring", {"start": v(34.94, -6.63) * mm, "mid": v(35.12, -5.56) * mm, "end": v(35.28, -4.49) * mm});
            skArc(sketch, "E73.trimOffspring", {"start": v(32.8, -13.75) * mm, "mid": v(33.2, -12.74) * mm, "end": v(33.57, -11.72) * mm});
            skArc(sketch, "E74.trimOffspring", {"start": v(29.22, -20.27) * mm, "mid": v(29.82, -19.37) * mm, "end": v(30.4, -18.45) * mm});
            skArc(sketch, "E75.trimOffspring", {"start": v(-11.72, 33.57) * mm, "mid": v(-12.74, 33.2) * mm, "end": v(-13.75, 32.8) * mm});
            skArc(sketch, "E76.trimOffspring", {"start": v(-18.45, 30.4) * mm, "mid": v(-19.37, 29.82) * mm, "end": v(-20.27, 29.22) * mm});
            skArc(sketch, "E77.trimOffspring", {"start": v(24.37, -25.9) * mm, "mid": v(25.14, -25.14) * mm, "end": v(25.9, -24.37) * mm});
            skArc(sketch, "E78.trimOffspring", {"start": v(18.45, -30.4) * mm, "mid": v(19.37, -29.82) * mm, "end": v(20.27, -29.22) * mm});
            skArc(sketch, "E79.trimOffspring", {"start": v(11.72, -33.57) * mm, "mid": v(12.74, -33.2) * mm, "end": v(13.75, -32.8) * mm});
            skArc(sketch, "E80.trimOffspring", {"start": v(4.49, -35.28) * mm, "mid": v(5.56, -35.12) * mm, "end": v(6.63, -34.94) * mm});
            skArc(sketch, "E81.trimOffspring", {"start": v(-2.94, -35.44) * mm, "mid": v(-1.86, -35.51) * mm, "end": v(-0.78, -35.55) * mm});
            skArc(sketch, "E82.trimOffspring", {"start": v(-10.25, -34.05) * mm, "mid": v(-9.2, -34.35) * mm, "end": v(-8.15, -34.61) * mm});
            skArc(sketch, "E83.trimOffspring", {"start": v(-17.1, -31.18) * mm, "mid": v(-16.14, -31.68) * mm, "end": v(-15.17, -32.16) * mm});
            skArc(sketch, "E84.trimOffspring", {"start": v(-23.21, -26.94) * mm, "mid": v(-22.38, -27.64) * mm, "end": v(-21.52, -28.3) * mm});
            skArc(sketch, "E85.trimOffspring", {"start": v(-28.3, -21.52) * mm, "mid": v(-27.64, -22.38) * mm, "end": v(-26.94, -23.21) * mm});
            skArc(sketch, "E86.trimOffspring", {"start": v(-32.16, -15.17) * mm, "mid": v(-31.68, -16.14) * mm, "end": v(-31.18, -17.1) * mm});
            skArc(sketch, "E87.trimOffspring", {"start": v(-34.61, -8.15) * mm, "mid": v(-34.35, -9.2) * mm, "end": v(-34.05, -10.25) * mm});
            skArc(sketch, "E88.trimOffspring", {"start": v(-35.55, -0.78) * mm, "mid": v(-35.51, -1.86) * mm, "end": v(-35.44, -2.94) * mm});
            skArc(sketch, "E89.trimOffspring", {"start": v(-34.94, 6.63) * mm, "mid": v(-35.12, 5.56) * mm, "end": v(-35.28, 4.49) * mm});
            skArc(sketch, "E90.trimOffspring", {"start": v(-32.8, 13.75) * mm, "mid": v(-33.2, 12.74) * mm, "end": v(-33.57, 11.72) * mm});
            skArc(sketch, "E91.trimOffspring", {"start": v(-29.22, 20.27) * mm, "mid": v(-29.82, 19.37) * mm, "end": v(-30.4, 18.45) * mm});
            skArc(sketch, "E92.trimOffspring", {"start": v(-24.37, 25.9) * mm, "mid": v(-25.14, 25.14) * mm, "end": v(-25.9, 24.37) * mm});
            skSolve(sketch);
        }
        {
            var Q0;
            Q0=makeQuery(id+"F2.imprint","IMPRINT",FACE,{"disambiguationData":[TD([[makeQuery(id+"F2.imprint","IMPRINT",EDGE,{"derivedFrom":sQuery(id+"F2.wireOp",EDGE,"E46")}),1.0]])]});
            var Q1;
            Q1=makeQuery(id+"F0.imprint","IMPRINT",FACE,{"disambiguationData":[TD([[makeQuery(id+"F0.imprint","IMPRINT",EDGE,{"derivedFrom":sQuery(id+"F0.wireOp",EDGE,"E1.trimOffspring")}),1.0]])]});
            var Q2;
            Q2=sQuery(id+"F0.wireOp",VERTEX,"E15.2.12.end");
            var Q3;
            Q3=sQuery(id+"F2.wireOp",VERTEX,"E50.MirrorCS.end");
            loft(context, id + "F3", {"sheetProfilesArray" : [{ "sheetProfileEntities" : qUnion([Q0]) }, { "sheetProfileEntities" : qUnion([Q1]) }], "matchConnections" : true, "connections" : [{ "connectionEntities" : qUnion([Q2, Q3]), "connectionEdgeQueries" : qUnion([]), "connectionEdgeParameters" : [] }]});
        }
        {
            var Q0;
            Q0=sQuery(id+"F0.wireOp",VERTEX,"E0.center");
            var Q1;
            Q1=makeQuery(id+"F3.opLoft","SWEPT_BODY",BODY,{"disambiguationData":[OSD([makeQuery(id+"F0.imprint","IMPRINT",FACE,{"disambiguationData":[TD([[makeQuery(id+"F0.imprint","IMPRINT",EDGE,{"derivedFrom":sQuery(id+"F0.wireOp",EDGE,"E1.trimOffspring")}),1.0]])]}),makeQuery(id+"F2.imprint","IMPRINT",FACE,{"disambiguationData":[TD([[makeQuery(id+"F2.imprint","IMPRINT",EDGE,{"derivedFrom":sQuery(id+"F2.wireOp",EDGE,"E46")}),1.0]])]})])]});
            hole(context, id + "F4", {"style" : HoleStyle.SIMPLE, "endStyle" : HoleEndStyle.THROUGH, "oppositeDirection" : true, "holeDiameter" : 12.7 * mm, "tappedDepth" : 12.7 * mm, "tapClearance" : 3, "locations" : qUnion([Q0]), "scope" : qUnion([Q1])});
        }
    });
